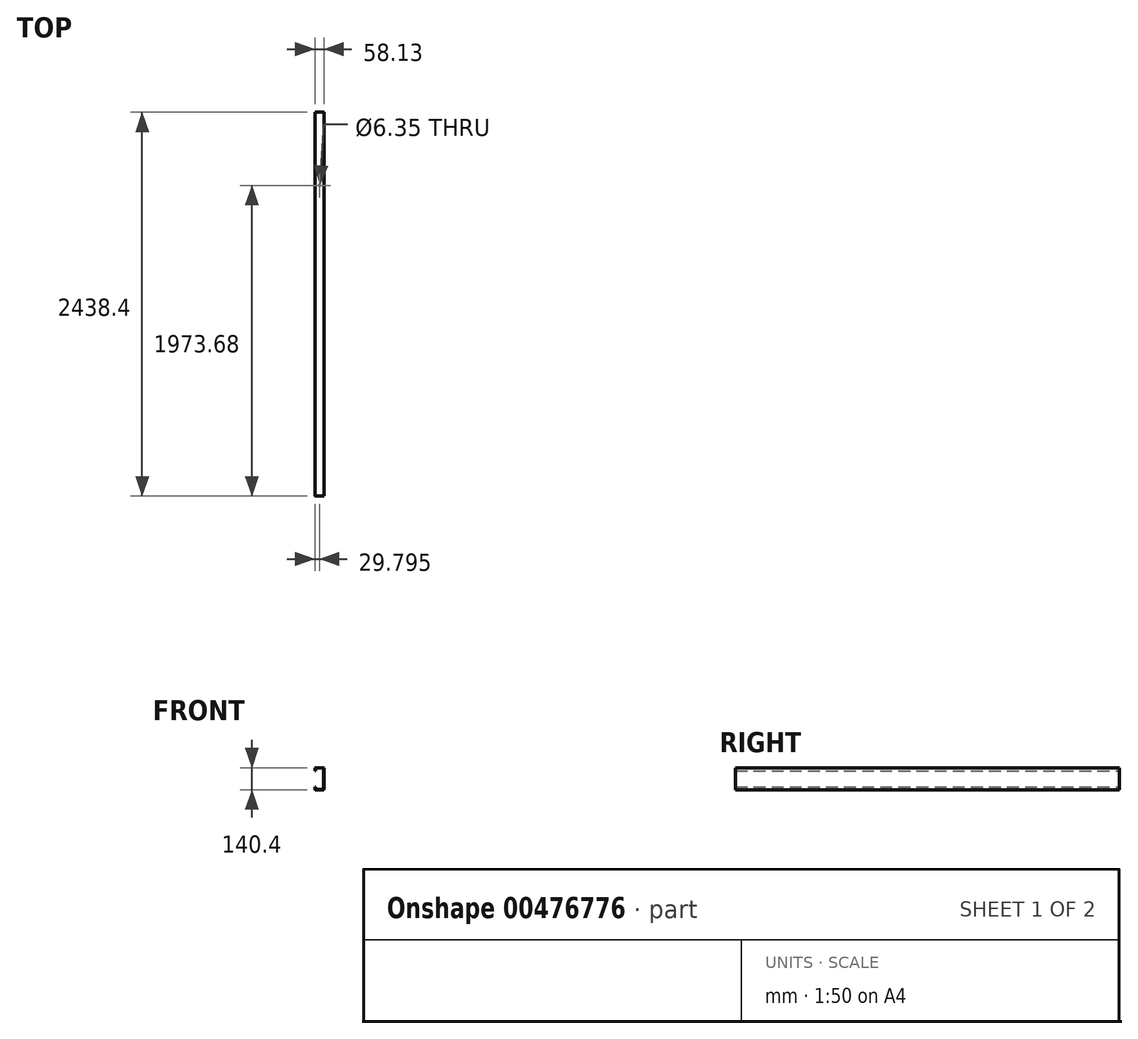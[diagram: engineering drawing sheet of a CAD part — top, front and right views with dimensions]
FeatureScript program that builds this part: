
annotation { "Feature Type Name" : "Feature", "Feature Type Description" : "" }
export const myFeature = defineFeature(function(context is Context, id is Id, definition is map)
    precondition{}
    {
        {
            var Q0;
            Q0=qCreatedBy(makeId("Front.planeOp"),FACE);
            var sketch = newSketch(context, id + "F0", { "sketchPlane" : qUnion([Q0])});
            skLineSegment(sketch, "E0", {"start": v(-431.8, -558.8) * mm, "end": v(431.8, -558.8) * mm});
            skLineSegment(sketch, "E1", {"start": v(431.8, -558.8) * mm, "end": v(431.8, 558.8) * mm});
            skLineSegment(sketch, "E2", {"start": v(431.8, 558.8) * mm, "end": v(-431.8, 558.8) * mm});
            skLineSegment(sketch, "E3", {"start": v(-431.8, 558.8) * mm, "end": v(-431.8, -558.8) * mm});
            skLineSegment(sketch, "E4", {"start": v(-381, -504.83) * mm, "end": v(381, -504.83) * mm});
            skLineSegment(sketch, "E5", {"start": v(381, -504.83) * mm, "end": v(381, 504.83) * mm});
            skLineSegment(sketch, "E6", {"start": v(381, 504.83) * mm, "end": v(360.7, 504.83) * mm});
            skLineSegment(sketch, "E7", {"start": v(265.82, 504.83) * mm, "end": v(-381, 504.83) * mm});
            skLineSegment(sketch, "E8", {"start": v(-381, 504.83) * mm, "end": v(-381, -504.83) * mm});
            skLineSegment(sketch, "E9", {"start": v(-381, -403.23) * mm, "end": v(381, -403.23) * mm});
            skLineSegment(sketch, "E10", {"start": v(-152.4, -403.23) * mm, "end": v(-152.4, -504.83) * mm});
            skLineSegment(sketch, "E11", {"start": v(152.4, -403.23) * mm, "end": v(152.4, -504.83) * mm});
            skLineSegment(sketch, "E12", {"start": v(349.12, 503.33) * mm, "end": v(324.77, 544.8) * mm});
            skLineSegment(sketch, "E13", {"start": v(324.92, 525.17) * mm, "end": v(343.26, 493.25) * mm});
            skLineSegment(sketch, "E14", {"start": v(345.3, 496.77) * mm, "end": v(323.11, 534.57) * mm});
            skLineSegment(sketch, "E15", {"start": v(351.17, 506.85) * mm, "end": v(327.06, 548.5) * mm});
            skLineSegment(sketch, "E16", {"start": v(335.24, 486.66) * mm, "end": v(339.43, 486.66) * mm});
            skLineSegment(sketch, "E17", {"start": v(323.53, 514.34) * mm, "end": v(339.43, 486.66) * mm});
            skLineSegment(sketch, "E18", {"start": v(324.77, 544.8) * mm, "end": v(303.2, 507.27) * mm});
            skLineSegment(sketch, "E19", {"start": v(323.11, 534.57) * mm, "end": v(305.2, 503.47) * mm});
            skLineSegment(sketch, "E20", {"start": v(303.02, 548.5) * mm, "end": v(279.32, 507.27) * mm});
            skLineSegment(sketch, "E21", {"start": v(305.2, 503.47) * mm, "end": v(281.51, 503.47) * mm});
            skLineSegment(sketch, "E22", {"start": v(303.2, 507.27) * mm, "end": v(279.32, 507.27) * mm});
            skLineSegment(sketch, "E23", {"start": v(287.46, 493.17) * mm, "end": v(311.53, 493.17) * mm});
            skLineSegment(sketch, "E24", {"start": v(285.48, 496.6) * mm, "end": v(309, 496.6) * mm});
            skLineSegment(sketch, "E25", {"start": v(315.3, 486.66) * mm, "end": v(291.22, 486.66) * mm});
            skLineSegment(sketch, "E26", {"start": v(281.51, 503.47) * mm, "end": v(285.48, 496.6) * mm});
            skLineSegment(sketch, "E27", {"start": v(287.46, 493.17) * mm, "end": v(291.22, 486.66) * mm});
            skLineSegment(sketch, "E28", {"start": v(309, 496.6) * mm, "end": v(324.92, 525.17) * mm});
            skLineSegment(sketch, "E29", {"start": v(311.53, 493.17) * mm, "end": v(323.53, 514.34) * mm});
            skLineSegment(sketch, "E30", {"start": v(325.28, 503.65) * mm, "end": v(315.3, 486.66) * mm});
            skLineSegment(sketch, "E31", {"start": v(319.7, 486.66) * mm, "end": v(326.89, 486.66) * mm});
            skLineSegment(sketch, "E32", {"start": v(319.7, 486.66) * mm, "end": v(323.3, 492.99) * mm});
            skLineSegment(sketch, "E33", {"start": v(335.24, 486.66) * mm, "end": v(325.28, 503.65) * mm});
            skLineSegment(sketch, "E34", {"start": v(323.3, 492.99) * mm, "end": v(326.89, 486.66) * mm});
            skLineSegment(sketch, "E35", {"start": v(327.06, 548.5) * mm, "end": v(303.02, 548.5) * mm});
            skLineSegment(sketch, "E36", {"start": v(343.26, 493.25) * mm, "end": v(345.3, 496.77) * mm});
            skLineSegment(sketch, "E37", {"start": v(349.12, 503.33) * mm, "end": v(351.17, 506.85) * mm});
            skCircle(sketch, "E38", {"center": v(350.6, 458.79) * mm, "radius": 1.85 * mm});
            skLineSegment(sketch, "E39", {"start": v(-201.65, 389.86) * mm, "end": v(-204.7, 389.86) * mm});
            skLineSegment(sketch, "E40", {"start": v(-201.65, 287.56) * mm, "end": v(-204.7, 287.56) * mm});
            skLineSegment(sketch, "E41", {"start": v(-204.7, 389.86) * mm, "end": v(-204.7, 405.1) * mm});
            skLineSegment(sketch, "E42", {"start": v(-201.65, 389.86) * mm, "end": v(-201.65, 405.1) * mm});
            skArc(sketch, "E43", {"start": v(-200.89, 405.86) * mm, "mid": v(-201.43, 405.64) * mm, "end": v(-201.65, 405.1) * mm});
            skArc(sketch, "E44", {"start": v(-200.89, 408.9) * mm, "mid": v(-203.58, 407.8) * mm, "end": v(-204.7, 405.1) * mm});
            skLineSegment(sketch, "E45", {"start": v(-200.89, 408.9) * mm, "end": v(-151.83, 408.9) * mm});
            skLineSegment(sketch, "E46", {"start": v(-200.89, 405.86) * mm, "end": v(-151.83, 405.86) * mm});
            skArc(sketch, "E47", {"start": v(-151.07, 405.1) * mm, "mid": v(-151.3, 405.64) * mm, "end": v(-151.83, 405.86) * mm});
            skArc(sketch, "E48", {"start": v(-148.02, 405.1) * mm, "mid": v(-149.14, 407.8) * mm, "end": v(-151.83, 408.9) * mm});
            skLineSegment(sketch, "E49", {"start": v(-148.02, 405.1) * mm, "end": v(-148.02, 272.32) * mm});
            skLineSegment(sketch, "E50", {"start": v(-151.07, 405.1) * mm, "end": v(-151.07, 272.32) * mm});
            skLineSegment(sketch, "E51", {"start": v(-204.7, 287.56) * mm, "end": v(-204.7, 273.15) * mm});
            skLineSegment(sketch, "E52", {"start": v(-201.65, 287.56) * mm, "end": v(-201.65, 273.15) * mm});
            skLineSegment(sketch, "E53", {"start": v(-200.06, 268.51) * mm, "end": v(-151.83, 268.51) * mm});
            skLineSegment(sketch, "E54", {"start": v(-200.06, 271.56) * mm, "end": v(-151.83, 271.56) * mm});
            skArc(sketch, "E55", {"start": v(-151.83, 271.56) * mm, "mid": v(-151.3, 271.79) * mm, "end": v(-151.07, 272.32) * mm});
            skArc(sketch, "E56", {"start": v(-151.83, 268.51) * mm, "mid": v(-149.14, 269.63) * mm, "end": v(-148.02, 272.32) * mm});
            skArc(sketch, "E57", {"start": v(-201.65, 273.15) * mm, "mid": v(-201.19, 272.03) * mm, "end": v(-200.06, 271.56) * mm});
            skArc(sketch, "E58", {"start": v(-204.7, 273.15) * mm, "mid": v(-203.34, 269.87) * mm, "end": v(-200.06, 268.51) * mm});
            skLineSegment(sketch, "E59", {"start": v(268.24, 192.18) * mm, "end": v(-275.4, 192.18) * mm});
            skLineSegment(sketch, "E60", {"start": v(-275.4, 267.58) * mm, "end": v(268.24, 267.58) * mm});
            skLineSegment(sketch, "E61", {"start": v(-275.4, 191.38) * mm, "end": v(268.24, 191.38) * mm});
            skLineSegment(sketch, "E62", {"start": v(-275.4, 189.56) * mm, "end": v(-275.4, 233.5) * mm});
            skLineSegment(sketch, "E63", {"start": v(-275.4, 238.46) * mm, "end": v(-275.4, 270.12) * mm});
            skLineSegment(sketch, "E64", {"start": v(-275.4, 233.5) * mm, "end": v(-264.27, 236) * mm});
            skLineSegment(sketch, "E65", {"start": v(-287.59, 236) * mm, "end": v(-275.4, 238.46) * mm});
            skLineSegment(sketch, "E66", {"start": v(-287.59, 236) * mm, "end": v(-264.27, 236) * mm});
            skLineSegment(sketch, "E67", {"start": v(268.24, 189.56) * mm, "end": v(268.24, 233.5) * mm});
            skLineSegment(sketch, "E68", {"start": v(268.24, 238.46) * mm, "end": v(268.24, 270.12) * mm});
            skLineSegment(sketch, "E69", {"start": v(268.24, 233.5) * mm, "end": v(279.38, 236) * mm});
            skLineSegment(sketch, "E70", {"start": v(256.06, 236) * mm, "end": v(268.24, 238.46) * mm});
            skLineSegment(sketch, "E71", {"start": v(256.06, 236) * mm, "end": v(279.38, 236) * mm});
            skLineSegment(sketch, "E72", {"start": v(267.92, 175.66) * mm, "end": v(267.92, 187.92) * mm});
            skLineSegment(sketch, "E73", {"start": v(-275.4, 175.66) * mm, "end": v(-275.4, 187.92) * mm});
            skLineSegment(sketch, "E74", {"start": v(131.2, 389.86) * mm, "end": v(128.15, 389.86) * mm});
            skLineSegment(sketch, "E75", {"start": v(131.2, 287.54) * mm, "end": v(128.15, 287.54) * mm});
            skLineSegment(sketch, "E76", {"start": v(128.15, 389.86) * mm, "end": v(128.15, 405.1) * mm});
            skLineSegment(sketch, "E77", {"start": v(131.2, 389.86) * mm, "end": v(131.2, 405.1) * mm});
            skArc(sketch, "E78", {"start": v(131.96, 408.9) * mm, "mid": v(129.27, 407.8) * mm, "end": v(128.15, 405.1) * mm});
            skLineSegment(sketch, "E79", {"start": v(131.96, 408.9) * mm, "end": v(182.96, 408.9) * mm});
            skLineSegment(sketch, "E80", {"start": v(131.96, 405.86) * mm, "end": v(182.96, 405.86) * mm});
            skArc(sketch, "E81", {"start": v(183.72, 405.1) * mm, "mid": v(183.5, 405.64) * mm, "end": v(182.96, 405.86) * mm});
            skArc(sketch, "E82", {"start": v(186.77, 405.1) * mm, "mid": v(185.65, 407.8) * mm, "end": v(182.96, 408.9) * mm});
            skLineSegment(sketch, "E83", {"start": v(186.77, 405.1) * mm, "end": v(186.77, 272.3) * mm});
            skLineSegment(sketch, "E84", {"start": v(183.72, 405.1) * mm, "end": v(183.72, 272.3) * mm});
            skLineSegment(sketch, "E85", {"start": v(128.15, 287.54) * mm, "end": v(128.15, 273.12) * mm});
            skLineSegment(sketch, "E86", {"start": v(131.2, 287.54) * mm, "end": v(131.2, 273.12) * mm});
            skLineSegment(sketch, "E87", {"start": v(132.79, 268.49) * mm, "end": v(182.96, 268.49) * mm});
            skLineSegment(sketch, "E88", {"start": v(132.79, 271.53) * mm, "end": v(182.96, 271.53) * mm});
            skArc(sketch, "E89", {"start": v(182.96, 271.53) * mm, "mid": v(183.5, 271.76) * mm, "end": v(183.72, 272.3) * mm});
            skArc(sketch, "E90", {"start": v(182.96, 268.49) * mm, "mid": v(185.65, 269.6) * mm, "end": v(186.77, 272.3) * mm});
            skArc(sketch, "E91", {"start": v(131.2, 273.12) * mm, "mid": v(131.67, 272) * mm, "end": v(132.79, 271.53) * mm});
            skArc(sketch, "E92", {"start": v(128.15, 273.12) * mm, "mid": v(129.51, 269.84) * mm, "end": v(132.79, 268.49) * mm});
            skLineSegment(sketch, "E93", {"start": v(-275.4, 266.78) * mm, "end": v(268.24, 266.78) * mm});
            skArc(sketch, "E94", {"start": v(131.96, 405.86) * mm, "mid": v(131.42, 405.64) * mm, "end": v(131.2, 405.1) * mm});
            skLineSegment(sketch, "E95", {"start": v(-148.02, 350.55) * mm, "end": v(-147.38, 350.55) * mm});
            skLineSegment(sketch, "E96", {"start": v(268.24, 220.63) * mm, "end": v(-275.4, 220.63) * mm});
            skLineSegment(sketch, "E97", {"start": v(-275.4, 219.83) * mm, "end": v(268.24, 219.83) * mm});
            skLineSegment(sketch, "E98", {"start": v(111.4, 219.88) * mm, "end": v(200.2, 219.88) * mm});
            skLineSegment(sketch, "E99", {"start": v(200.2, 219.88) * mm, "end": v(200.2, 218.1) * mm});
            skLineSegment(sketch, "E100", {"start": v(111.4, 219.88) * mm, "end": v(111.4, 218.1) * mm});
            skLineSegment(sketch, "E101", {"start": v(111.4, 218.1) * mm, "end": v(200.2, 218.1) * mm});
            skLineSegment(sketch, "E102", {"start": v(165.87, 216.24) * mm, "end": v(165.87, 217.5) * mm});
            skLineSegment(sketch, "E103", {"start": v(152.66, 216.24) * mm, "end": v(152.66, 217.5) * mm});
            skLineSegment(sketch, "E104", {"start": v(164.46, 211.81) * mm, "end": v(164.46, 216.24) * mm});
            skLineSegment(sketch, "E105", {"start": v(154.07, 211.81) * mm, "end": v(154.07, 216.24) * mm});
            skLineSegment(sketch, "E106", {"start": v(161.7, 259.32) * mm, "end": v(161.7, 260.34) * mm});
            skLineSegment(sketch, "E107", {"start": v(161.7, 261.14) * mm, "end": v(161.7, 262.16) * mm});
            skLineSegment(sketch, "E108", {"start": v(161.7, 262.95) * mm, "end": v(161.7, 263.97) * mm});
            skLineSegment(sketch, "E109", {"start": v(161.7, 264.76) * mm, "end": v(161.7, 265.78) * mm});
            skLineSegment(sketch, "E110", {"start": v(161.7, 266.58) * mm, "end": v(161.7, 267.6) * mm});
            skLineSegment(sketch, "E111", {"start": v(161.7, 268.39) * mm, "end": v(161.7, 269.41) * mm});
            skLineSegment(sketch, "E112", {"start": v(161.7, 270.2) * mm, "end": v(161.7, 271.22) * mm});
            skLineSegment(sketch, "E113", {"start": v(161.7, 272.02) * mm, "end": v(161.7, 273.04) * mm});
            skLineSegment(sketch, "E114", {"start": v(161.7, 273.83) * mm, "end": v(161.7, 274.85) * mm});
            skLineSegment(sketch, "E115", {"start": v(161.7, 275.64) * mm, "end": v(161.7, 276.67) * mm});
            skLineSegment(sketch, "E116", {"start": v(161.7, 277.46) * mm, "end": v(161.7, 278.48) * mm});
            skLineSegment(sketch, "E117", {"start": v(156.83, 257.5) * mm, "end": v(156.83, 258.53) * mm});
            skLineSegment(sketch, "E118", {"start": v(156.83, 259.32) * mm, "end": v(156.83, 260.34) * mm});
            skLineSegment(sketch, "E119", {"start": v(156.83, 261.14) * mm, "end": v(156.83, 262.16) * mm});
            skLineSegment(sketch, "E120", {"start": v(156.83, 262.95) * mm, "end": v(156.83, 263.97) * mm});
            skLineSegment(sketch, "E121", {"start": v(156.83, 264.76) * mm, "end": v(156.83, 265.78) * mm});
            skLineSegment(sketch, "E122", {"start": v(156.83, 266.58) * mm, "end": v(156.83, 267.6) * mm});
            skLineSegment(sketch, "E123", {"start": v(156.83, 268.39) * mm, "end": v(156.83, 269.41) * mm});
            skLineSegment(sketch, "E124", {"start": v(156.83, 270.2) * mm, "end": v(156.83, 271.22) * mm});
            skLineSegment(sketch, "E125", {"start": v(156.83, 272.02) * mm, "end": v(156.83, 273.04) * mm});
            skLineSegment(sketch, "E126", {"start": v(156.83, 273.83) * mm, "end": v(156.83, 274.85) * mm});
            skLineSegment(sketch, "E127", {"start": v(156.83, 275.64) * mm, "end": v(156.83, 276.67) * mm});
            skLineSegment(sketch, "E128", {"start": v(156.14, 258.93) * mm, "end": v(156.83, 258.53) * mm});
            skLineSegment(sketch, "E129", {"start": v(156.14, 258.93) * mm, "end": v(156.83, 259.32) * mm});
            skLineSegment(sketch, "E130", {"start": v(156.14, 260.74) * mm, "end": v(156.83, 260.34) * mm});
            skLineSegment(sketch, "E131", {"start": v(156.14, 260.74) * mm, "end": v(156.83, 261.14) * mm});
            skLineSegment(sketch, "E132", {"start": v(162.39, 260.74) * mm, "end": v(161.7, 260.34) * mm});
            skLineSegment(sketch, "E133", {"start": v(162.39, 260.74) * mm, "end": v(161.7, 261.14) * mm});
            skLineSegment(sketch, "E134", {"start": v(162.39, 262.55) * mm, "end": v(161.7, 262.16) * mm});
            skLineSegment(sketch, "E135", {"start": v(162.39, 262.55) * mm, "end": v(161.7, 262.95) * mm});
            skLineSegment(sketch, "E136", {"start": v(156.14, 258.93) * mm, "end": v(162.39, 260.74) * mm});
            skLineSegment(sketch, "E137", {"start": v(156.14, 260.74) * mm, "end": v(162.39, 262.55) * mm});
            skLineSegment(sketch, "E138", {"start": v(156.83, 258.53) * mm, "end": v(161.7, 260.34) * mm});
            skLineSegment(sketch, "E139", {"start": v(156.83, 259.32) * mm, "end": v(161.7, 261.14) * mm});
            skLineSegment(sketch, "E140", {"start": v(156.83, 260.34) * mm, "end": v(161.7, 262.16) * mm});
            skLineSegment(sketch, "E141", {"start": v(156.83, 261.14) * mm, "end": v(161.7, 262.95) * mm});
            skLineSegment(sketch, "E142", {"start": v(156.14, 262.55) * mm, "end": v(156.83, 262.16) * mm});
            skLineSegment(sketch, "E143", {"start": v(156.14, 262.55) * mm, "end": v(156.83, 262.95) * mm});
            skLineSegment(sketch, "E144", {"start": v(156.14, 264.37) * mm, "end": v(156.83, 263.97) * mm});
            skLineSegment(sketch, "E145", {"start": v(156.14, 264.37) * mm, "end": v(156.83, 264.76) * mm});
            skLineSegment(sketch, "E146", {"start": v(162.39, 264.37) * mm, "end": v(161.7, 263.97) * mm});
            skLineSegment(sketch, "E147", {"start": v(162.39, 264.37) * mm, "end": v(161.7, 264.76) * mm});
            skLineSegment(sketch, "E148", {"start": v(162.39, 266.18) * mm, "end": v(161.7, 265.78) * mm});
            skLineSegment(sketch, "E149", {"start": v(162.39, 266.18) * mm, "end": v(161.7, 266.58) * mm});
            skLineSegment(sketch, "E150", {"start": v(156.14, 262.55) * mm, "end": v(162.39, 264.37) * mm});
            skLineSegment(sketch, "E151", {"start": v(156.14, 264.37) * mm, "end": v(162.39, 266.18) * mm});
            skLineSegment(sketch, "E152", {"start": v(156.83, 262.16) * mm, "end": v(161.7, 263.97) * mm});
            skLineSegment(sketch, "E153", {"start": v(156.83, 262.95) * mm, "end": v(161.7, 264.76) * mm});
            skLineSegment(sketch, "E154", {"start": v(156.83, 263.97) * mm, "end": v(161.7, 265.78) * mm});
            skLineSegment(sketch, "E155", {"start": v(156.83, 264.76) * mm, "end": v(161.7, 266.58) * mm});
            skLineSegment(sketch, "E156", {"start": v(156.14, 266.18) * mm, "end": v(156.83, 265.78) * mm});
            skLineSegment(sketch, "E157", {"start": v(156.14, 266.18) * mm, "end": v(156.83, 266.58) * mm});
            skLineSegment(sketch, "E158", {"start": v(162.39, 268) * mm, "end": v(161.7, 267.6) * mm});
            skLineSegment(sketch, "E159", {"start": v(162.39, 268) * mm, "end": v(161.7, 268.39) * mm});
            skLineSegment(sketch, "E160", {"start": v(156.14, 266.18) * mm, "end": v(162.39, 268) * mm});
            skLineSegment(sketch, "E161", {"start": v(156.83, 265.78) * mm, "end": v(161.7, 267.6) * mm});
            skLineSegment(sketch, "E162", {"start": v(156.83, 266.58) * mm, "end": v(161.7, 268.39) * mm});
            skLineSegment(sketch, "E163", {"start": v(156.14, 268) * mm, "end": v(156.83, 267.6) * mm});
            skLineSegment(sketch, "E164", {"start": v(156.14, 268) * mm, "end": v(156.83, 268.39) * mm});
            skLineSegment(sketch, "E165", {"start": v(156.14, 269.8) * mm, "end": v(156.83, 269.41) * mm});
            skLineSegment(sketch, "E166", {"start": v(156.14, 269.8) * mm, "end": v(156.83, 270.2) * mm});
            skLineSegment(sketch, "E167", {"start": v(162.39, 269.8) * mm, "end": v(161.7, 269.41) * mm});
            skLineSegment(sketch, "E168", {"start": v(162.39, 269.8) * mm, "end": v(161.7, 270.2) * mm});
            skLineSegment(sketch, "E169", {"start": v(162.39, 271.62) * mm, "end": v(161.7, 271.22) * mm});
            skLineSegment(sketch, "E170", {"start": v(162.39, 271.62) * mm, "end": v(161.7, 272.02) * mm});
            skLineSegment(sketch, "E171", {"start": v(156.14, 268) * mm, "end": v(162.39, 269.8) * mm});
            skLineSegment(sketch, "E172", {"start": v(156.14, 269.8) * mm, "end": v(162.39, 271.62) * mm});
            skLineSegment(sketch, "E173", {"start": v(156.83, 267.6) * mm, "end": v(161.7, 269.41) * mm});
            skLineSegment(sketch, "E174", {"start": v(156.83, 268.39) * mm, "end": v(161.7, 270.2) * mm});
            skLineSegment(sketch, "E175", {"start": v(156.83, 269.41) * mm, "end": v(161.7, 271.22) * mm});
            skLineSegment(sketch, "E176", {"start": v(156.83, 270.2) * mm, "end": v(161.7, 272.02) * mm});
            skLineSegment(sketch, "E177", {"start": v(156.14, 271.62) * mm, "end": v(156.83, 271.22) * mm});
            skLineSegment(sketch, "E178", {"start": v(156.14, 271.62) * mm, "end": v(156.83, 272.02) * mm});
            skLineSegment(sketch, "E179", {"start": v(156.14, 273.43) * mm, "end": v(156.83, 273.04) * mm});
            skLineSegment(sketch, "E180", {"start": v(156.14, 273.43) * mm, "end": v(156.83, 273.83) * mm});
            skLineSegment(sketch, "E181", {"start": v(162.39, 273.43) * mm, "end": v(161.7, 273.04) * mm});
            skLineSegment(sketch, "E182", {"start": v(162.39, 273.43) * mm, "end": v(161.7, 273.83) * mm});
            skLineSegment(sketch, "E183", {"start": v(162.39, 275.25) * mm, "end": v(161.7, 274.85) * mm});
            skLineSegment(sketch, "E184", {"start": v(162.39, 275.25) * mm, "end": v(161.7, 275.64) * mm});
            skLineSegment(sketch, "E185", {"start": v(156.14, 271.62) * mm, "end": v(162.39, 273.43) * mm});
            skLineSegment(sketch, "E186", {"start": v(156.14, 273.43) * mm, "end": v(162.39, 275.25) * mm});
            skLineSegment(sketch, "E187", {"start": v(156.83, 271.22) * mm, "end": v(161.7, 273.04) * mm});
            skLineSegment(sketch, "E188", {"start": v(156.83, 272.02) * mm, "end": v(161.7, 273.83) * mm});
            skLineSegment(sketch, "E189", {"start": v(156.83, 273.04) * mm, "end": v(161.7, 274.85) * mm});
            skLineSegment(sketch, "E190", {"start": v(156.83, 273.83) * mm, "end": v(161.7, 275.64) * mm});
            skLineSegment(sketch, "E191", {"start": v(156.14, 275.25) * mm, "end": v(156.83, 274.85) * mm});
            skLineSegment(sketch, "E192", {"start": v(156.14, 275.25) * mm, "end": v(156.83, 275.64) * mm});
            skLineSegment(sketch, "E193", {"start": v(156.14, 277.06) * mm, "end": v(156.83, 276.67) * mm});
            skLineSegment(sketch, "E194", {"start": v(156.14, 277.06) * mm, "end": v(156.83, 277.46) * mm});
            skLineSegment(sketch, "E195", {"start": v(162.39, 277.06) * mm, "end": v(161.7, 276.67) * mm});
            skLineSegment(sketch, "E196", {"start": v(162.39, 277.06) * mm, "end": v(161.7, 277.46) * mm});
            skLineSegment(sketch, "E197", {"start": v(162.39, 278.87) * mm, "end": v(161.7, 278.48) * mm});
            skLineSegment(sketch, "E198", {"start": v(162.39, 278.87) * mm, "end": v(161.7, 279.27) * mm});
            skLineSegment(sketch, "E199", {"start": v(156.14, 275.25) * mm, "end": v(162.39, 277.06) * mm});
            skLineSegment(sketch, "E200", {"start": v(156.14, 277.06) * mm, "end": v(162.39, 278.87) * mm});
            skLineSegment(sketch, "E201", {"start": v(156.83, 274.85) * mm, "end": v(161.7, 276.67) * mm});
            skLineSegment(sketch, "E202", {"start": v(156.83, 275.64) * mm, "end": v(161.7, 277.46) * mm});
            skLineSegment(sketch, "E203", {"start": v(156.83, 276.67) * mm, "end": v(161.7, 278.48) * mm});
            skLineSegment(sketch, "E204", {"start": v(156.83, 277.46) * mm, "end": v(161.7, 279.27) * mm});
            skLineSegment(sketch, "E205", {"start": v(152.66, 217.5) * mm, "end": v(165.87, 217.5) * mm});
            skLineSegment(sketch, "E206", {"start": v(152.66, 216.24) * mm, "end": v(165.87, 216.24) * mm});
            skLineSegment(sketch, "E207", {"start": v(154.77, 211.41) * mm, "end": v(163.76, 211.41) * mm});
            skLineSegment(sketch, "E208", {"start": v(156.67, 211.81) * mm, "end": v(156.67, 216.24) * mm});
            skLineSegment(sketch, "E209", {"start": v(161.86, 211.81) * mm, "end": v(161.86, 216.24) * mm});
            skLineSegment(sketch, "E210", {"start": v(154.77, 211.41) * mm, "end": v(154.07, 211.81) * mm});
            skLineSegment(sketch, "E211", {"start": v(163.76, 211.41) * mm, "end": v(164.46, 211.81) * mm});
            skLineSegment(sketch, "E212", {"start": v(161.16, 211.41) * mm, "end": v(161.86, 211.81) * mm});
            skLineSegment(sketch, "E213", {"start": v(155.97, 211.41) * mm, "end": v(156.67, 211.81) * mm});
            skLineSegment(sketch, "E214", {"start": v(162.56, 211.41) * mm, "end": v(161.86, 211.81) * mm});
            skLineSegment(sketch, "E215", {"start": v(157.36, 211.41) * mm, "end": v(156.67, 211.81) * mm});
            skLineSegment(sketch, "E216", {"start": v(156.83, 277.46) * mm, "end": v(156.83, 288.94) * mm});
            skLineSegment(sketch, "E217", {"start": v(161.05, 279.03) * mm, "end": v(161.05, 288.94) * mm});
            skLineSegment(sketch, "E218", {"start": v(158.94, 290.16) * mm, "end": v(156.83, 288.94) * mm});
            skLineSegment(sketch, "E219", {"start": v(158.94, 290.16) * mm, "end": v(161.05, 288.94) * mm});
            skLineSegment(sketch, "E220", {"start": v(158.94, 290.16) * mm, "end": v(158.94, 280.63) * mm});
            skArc(sketch, "E221", {"start": v(158.94, 280.63) * mm, "mid": v(159.28, 279.49) * mm, "end": v(160.18, 278.7) * mm});
            skLineSegment(sketch, "E222", {"start": v(156.14, 257.11) * mm, "end": v(156.83, 256.72) * mm});
            skLineSegment(sketch, "E223", {"start": v(156.14, 257.11) * mm, "end": v(156.83, 257.5) * mm});
            skLineSegment(sketch, "E224", {"start": v(162.39, 258.93) * mm, "end": v(161.7, 258.53) * mm});
            skLineSegment(sketch, "E225", {"start": v(162.39, 258.93) * mm, "end": v(161.7, 259.32) * mm});
            skLineSegment(sketch, "E226", {"start": v(156.14, 257.11) * mm, "end": v(162.39, 258.93) * mm});
            skLineSegment(sketch, "E227", {"start": v(156.83, 256.72) * mm, "end": v(161.7, 258.53) * mm});
            skLineSegment(sketch, "E228", {"start": v(156.83, 257.5) * mm, "end": v(161.7, 259.32) * mm});
            skLineSegment(sketch, "E229", {"start": v(156.83, 256.72) * mm, "end": v(156.83, 217.5) * mm});
            skLineSegment(sketch, "E230", {"start": v(161.7, 258.53) * mm, "end": v(161.7, 217.5) * mm});
            skLineSegment(sketch, "E231", {"start": v(-224.84, 219.88) * mm, "end": v(-136.05, 219.88) * mm});
            skLineSegment(sketch, "E232", {"start": v(-224.84, 218.1) * mm, "end": v(-136.05, 218.1) * mm});
            skLineSegment(sketch, "E233", {"start": v(-136.05, 219.88) * mm, "end": v(-136.05, 218.1) * mm});
            skLineSegment(sketch, "E234", {"start": v(-224.84, 219.88) * mm, "end": v(-224.84, 218.1) * mm});
            skLineSegment(sketch, "E235", {"start": v(-170.37, 216.24) * mm, "end": v(-170.37, 217.5) * mm});
            skLineSegment(sketch, "E236", {"start": v(-183.58, 216.24) * mm, "end": v(-183.58, 217.5) * mm});
            skLineSegment(sketch, "E237", {"start": v(-171.78, 211.81) * mm, "end": v(-171.78, 216.24) * mm});
            skLineSegment(sketch, "E238", {"start": v(-182.17, 211.81) * mm, "end": v(-182.17, 216.24) * mm});
            skLineSegment(sketch, "E239", {"start": v(-174.54, 259.32) * mm, "end": v(-174.54, 260.34) * mm});
            skLineSegment(sketch, "E240", {"start": v(-174.54, 261.14) * mm, "end": v(-174.54, 262.16) * mm});
            skLineSegment(sketch, "E241", {"start": v(-174.54, 262.95) * mm, "end": v(-174.54, 263.97) * mm});
            skLineSegment(sketch, "E242", {"start": v(-174.54, 264.76) * mm, "end": v(-174.54, 265.78) * mm});
            skLineSegment(sketch, "E243", {"start": v(-174.54, 266.58) * mm, "end": v(-174.54, 267.6) * mm});
            skLineSegment(sketch, "E244", {"start": v(-174.54, 268.39) * mm, "end": v(-174.54, 269.41) * mm});
            skLineSegment(sketch, "E245", {"start": v(-174.54, 270.2) * mm, "end": v(-174.54, 271.22) * mm});
            skLineSegment(sketch, "E246", {"start": v(-174.54, 272.02) * mm, "end": v(-174.54, 273.04) * mm});
            skLineSegment(sketch, "E247", {"start": v(-174.54, 273.83) * mm, "end": v(-174.54, 274.85) * mm});
            skLineSegment(sketch, "E248", {"start": v(-174.54, 275.64) * mm, "end": v(-174.54, 276.67) * mm});
            skLineSegment(sketch, "E249", {"start": v(-174.54, 277.46) * mm, "end": v(-174.54, 278.48) * mm});
            skLineSegment(sketch, "E250", {"start": v(-179.41, 257.5) * mm, "end": v(-179.41, 258.53) * mm});
            skLineSegment(sketch, "E251", {"start": v(-179.41, 259.32) * mm, "end": v(-179.41, 260.34) * mm});
            skLineSegment(sketch, "E252", {"start": v(-179.41, 261.14) * mm, "end": v(-179.41, 262.16) * mm});
            skLineSegment(sketch, "E253", {"start": v(-179.41, 262.95) * mm, "end": v(-179.41, 263.97) * mm});
            skLineSegment(sketch, "E254", {"start": v(-179.41, 264.76) * mm, "end": v(-179.41, 265.78) * mm});
            skLineSegment(sketch, "E255", {"start": v(-179.41, 266.58) * mm, "end": v(-179.41, 267.6) * mm});
            skLineSegment(sketch, "E256", {"start": v(-179.41, 268.39) * mm, "end": v(-179.41, 269.41) * mm});
            skLineSegment(sketch, "E257", {"start": v(-179.41, 270.2) * mm, "end": v(-179.41, 271.22) * mm});
            skLineSegment(sketch, "E258", {"start": v(-179.41, 272.02) * mm, "end": v(-179.41, 273.04) * mm});
            skLineSegment(sketch, "E259", {"start": v(-179.41, 273.83) * mm, "end": v(-179.41, 274.85) * mm});
            skLineSegment(sketch, "E260", {"start": v(-179.41, 275.64) * mm, "end": v(-179.41, 276.67) * mm});
            skLineSegment(sketch, "E261", {"start": v(-180.1, 258.93) * mm, "end": v(-179.41, 258.53) * mm});
            skLineSegment(sketch, "E262", {"start": v(-180.1, 258.93) * mm, "end": v(-179.41, 259.32) * mm});
            skLineSegment(sketch, "E263", {"start": v(-180.1, 260.74) * mm, "end": v(-179.41, 260.34) * mm});
            skLineSegment(sketch, "E264", {"start": v(-180.1, 260.74) * mm, "end": v(-179.41, 261.14) * mm});
            skLineSegment(sketch, "E265", {"start": v(-173.85, 260.74) * mm, "end": v(-174.54, 260.34) * mm});
            skLineSegment(sketch, "E266", {"start": v(-173.85, 260.74) * mm, "end": v(-174.54, 261.14) * mm});
            skLineSegment(sketch, "E267", {"start": v(-173.85, 262.55) * mm, "end": v(-174.54, 262.16) * mm});
            skLineSegment(sketch, "E268", {"start": v(-173.85, 262.55) * mm, "end": v(-174.54, 262.95) * mm});
            skLineSegment(sketch, "E269", {"start": v(-180.1, 258.93) * mm, "end": v(-173.85, 260.74) * mm});
            skLineSegment(sketch, "E270", {"start": v(-180.1, 260.74) * mm, "end": v(-173.85, 262.55) * mm});
            skLineSegment(sketch, "E271", {"start": v(-179.41, 258.53) * mm, "end": v(-174.54, 260.34) * mm});
            skLineSegment(sketch, "E272", {"start": v(-179.41, 259.32) * mm, "end": v(-174.54, 261.14) * mm});
            skLineSegment(sketch, "E273", {"start": v(-179.41, 260.34) * mm, "end": v(-174.54, 262.16) * mm});
            skLineSegment(sketch, "E274", {"start": v(-179.41, 261.14) * mm, "end": v(-174.54, 262.95) * mm});
            skLineSegment(sketch, "E275", {"start": v(-180.1, 262.55) * mm, "end": v(-179.41, 262.16) * mm});
            skLineSegment(sketch, "E276", {"start": v(-180.1, 262.55) * mm, "end": v(-179.41, 262.95) * mm});
            skLineSegment(sketch, "E277", {"start": v(-180.1, 264.37) * mm, "end": v(-179.41, 263.97) * mm});
            skLineSegment(sketch, "E278", {"start": v(-180.1, 264.37) * mm, "end": v(-179.41, 264.76) * mm});
            skLineSegment(sketch, "E279", {"start": v(-173.85, 264.37) * mm, "end": v(-174.54, 263.97) * mm});
            skLineSegment(sketch, "E280", {"start": v(-173.85, 264.37) * mm, "end": v(-174.54, 264.76) * mm});
            skLineSegment(sketch, "E281", {"start": v(-173.85, 266.18) * mm, "end": v(-174.54, 265.78) * mm});
            skLineSegment(sketch, "E282", {"start": v(-173.85, 266.18) * mm, "end": v(-174.54, 266.58) * mm});
            skLineSegment(sketch, "E283", {"start": v(-180.1, 262.55) * mm, "end": v(-173.85, 264.37) * mm});
            skLineSegment(sketch, "E284", {"start": v(-180.1, 264.37) * mm, "end": v(-173.85, 266.18) * mm});
            skLineSegment(sketch, "E285", {"start": v(-179.41, 262.16) * mm, "end": v(-174.54, 263.97) * mm});
            skLineSegment(sketch, "E286", {"start": v(-179.41, 262.95) * mm, "end": v(-174.54, 264.76) * mm});
            skLineSegment(sketch, "E287", {"start": v(-179.41, 263.97) * mm, "end": v(-174.54, 265.78) * mm});
            skLineSegment(sketch, "E288", {"start": v(-179.41, 264.76) * mm, "end": v(-174.54, 266.58) * mm});
            skLineSegment(sketch, "E289", {"start": v(-180.1, 266.18) * mm, "end": v(-179.41, 265.78) * mm});
            skLineSegment(sketch, "E290", {"start": v(-180.1, 266.18) * mm, "end": v(-179.41, 266.58) * mm});
            skLineSegment(sketch, "E291", {"start": v(-173.85, 268) * mm, "end": v(-174.54, 267.6) * mm});
            skLineSegment(sketch, "E292", {"start": v(-173.85, 268) * mm, "end": v(-174.54, 268.39) * mm});
            skLineSegment(sketch, "E293", {"start": v(-180.1, 266.18) * mm, "end": v(-173.85, 268) * mm});
            skLineSegment(sketch, "E294", {"start": v(-179.41, 265.78) * mm, "end": v(-174.54, 267.6) * mm});
            skLineSegment(sketch, "E295", {"start": v(-179.41, 266.58) * mm, "end": v(-174.54, 268.39) * mm});
            skLineSegment(sketch, "E296", {"start": v(-180.1, 268) * mm, "end": v(-179.41, 267.6) * mm});
            skLineSegment(sketch, "E297", {"start": v(-180.1, 268) * mm, "end": v(-179.41, 268.39) * mm});
            skLineSegment(sketch, "E298", {"start": v(-180.1, 269.8) * mm, "end": v(-179.41, 269.41) * mm});
            skLineSegment(sketch, "E299", {"start": v(-180.1, 269.8) * mm, "end": v(-179.41, 270.2) * mm});
            skLineSegment(sketch, "E300", {"start": v(-173.85, 269.8) * mm, "end": v(-174.54, 269.41) * mm});
            skLineSegment(sketch, "E301", {"start": v(-173.85, 269.8) * mm, "end": v(-174.54, 270.2) * mm});
            skLineSegment(sketch, "E302", {"start": v(-173.85, 271.62) * mm, "end": v(-174.54, 271.22) * mm});
            skLineSegment(sketch, "E303", {"start": v(-173.85, 271.62) * mm, "end": v(-174.54, 272.02) * mm});
            skLineSegment(sketch, "E304", {"start": v(-180.1, 268) * mm, "end": v(-173.85, 269.8) * mm});
            skLineSegment(sketch, "E305", {"start": v(-180.1, 269.8) * mm, "end": v(-173.85, 271.62) * mm});
            skLineSegment(sketch, "E306", {"start": v(-179.41, 267.6) * mm, "end": v(-174.54, 269.41) * mm});
            skLineSegment(sketch, "E307", {"start": v(-179.41, 268.39) * mm, "end": v(-174.54, 270.2) * mm});
            skLineSegment(sketch, "E308", {"start": v(-179.41, 269.41) * mm, "end": v(-174.54, 271.22) * mm});
            skLineSegment(sketch, "E309", {"start": v(-179.41, 270.2) * mm, "end": v(-174.54, 272.02) * mm});
            skLineSegment(sketch, "E310", {"start": v(-180.1, 271.62) * mm, "end": v(-179.41, 271.22) * mm});
            skLineSegment(sketch, "E311", {"start": v(-180.1, 271.62) * mm, "end": v(-179.41, 272.02) * mm});
            skLineSegment(sketch, "E312", {"start": v(-180.1, 273.43) * mm, "end": v(-179.41, 273.04) * mm});
            skLineSegment(sketch, "E313", {"start": v(-180.1, 273.43) * mm, "end": v(-179.41, 273.83) * mm});
            skLineSegment(sketch, "E314", {"start": v(-173.85, 273.43) * mm, "end": v(-174.54, 273.04) * mm});
            skLineSegment(sketch, "E315", {"start": v(-173.85, 273.43) * mm, "end": v(-174.54, 273.83) * mm});
            skLineSegment(sketch, "E316", {"start": v(-173.85, 275.25) * mm, "end": v(-174.54, 274.85) * mm});
            skLineSegment(sketch, "E317", {"start": v(-173.85, 275.25) * mm, "end": v(-174.54, 275.64) * mm});
            skLineSegment(sketch, "E318", {"start": v(-180.1, 271.62) * mm, "end": v(-173.85, 273.43) * mm});
            skLineSegment(sketch, "E319", {"start": v(-180.1, 273.43) * mm, "end": v(-173.85, 275.25) * mm});
            skLineSegment(sketch, "E320", {"start": v(-179.41, 271.22) * mm, "end": v(-174.54, 273.04) * mm});
            skLineSegment(sketch, "E321", {"start": v(-179.41, 272.02) * mm, "end": v(-174.54, 273.83) * mm});
            skLineSegment(sketch, "E322", {"start": v(-179.41, 273.04) * mm, "end": v(-174.54, 274.85) * mm});
            skLineSegment(sketch, "E323", {"start": v(-179.41, 273.83) * mm, "end": v(-174.54, 275.64) * mm});
            skLineSegment(sketch, "E324", {"start": v(-180.1, 275.25) * mm, "end": v(-179.41, 274.85) * mm});
            skLineSegment(sketch, "E325", {"start": v(-180.1, 275.25) * mm, "end": v(-179.41, 275.64) * mm});
            skLineSegment(sketch, "E326", {"start": v(-180.1, 277.06) * mm, "end": v(-179.41, 276.67) * mm});
            skLineSegment(sketch, "E327", {"start": v(-180.1, 277.06) * mm, "end": v(-179.41, 277.46) * mm});
            skLineSegment(sketch, "E328", {"start": v(-173.85, 277.06) * mm, "end": v(-174.54, 276.67) * mm});
            skLineSegment(sketch, "E329", {"start": v(-173.85, 277.06) * mm, "end": v(-174.54, 277.46) * mm});
            skLineSegment(sketch, "E330", {"start": v(-173.85, 278.87) * mm, "end": v(-174.54, 278.48) * mm});
            skLineSegment(sketch, "E331", {"start": v(-173.85, 278.87) * mm, "end": v(-174.54, 279.27) * mm});
            skLineSegment(sketch, "E332", {"start": v(-180.1, 275.25) * mm, "end": v(-173.85, 277.06) * mm});
            skLineSegment(sketch, "E333", {"start": v(-180.1, 277.06) * mm, "end": v(-173.85, 278.87) * mm});
            skLineSegment(sketch, "E334", {"start": v(-179.41, 274.85) * mm, "end": v(-174.54, 276.67) * mm});
            skLineSegment(sketch, "E335", {"start": v(-179.41, 275.64) * mm, "end": v(-174.54, 277.46) * mm});
            skLineSegment(sketch, "E336", {"start": v(-179.41, 276.67) * mm, "end": v(-174.54, 278.48) * mm});
            skLineSegment(sketch, "E337", {"start": v(-179.41, 277.46) * mm, "end": v(-174.54, 279.27) * mm});
            skLineSegment(sketch, "E338", {"start": v(-183.58, 217.5) * mm, "end": v(-170.37, 217.5) * mm});
            skLineSegment(sketch, "E339", {"start": v(-183.58, 216.24) * mm, "end": v(-170.37, 216.24) * mm});
            skLineSegment(sketch, "E340", {"start": v(-181.47, 211.41) * mm, "end": v(-172.48, 211.41) * mm});
            skLineSegment(sketch, "E341", {"start": v(-179.57, 211.81) * mm, "end": v(-179.57, 216.24) * mm});
            skLineSegment(sketch, "E342", {"start": v(-174.38, 211.81) * mm, "end": v(-174.38, 216.24) * mm});
            skLineSegment(sketch, "E343", {"start": v(-181.47, 211.41) * mm, "end": v(-182.17, 211.81) * mm});
            skLineSegment(sketch, "E344", {"start": v(-172.48, 211.41) * mm, "end": v(-171.78, 211.81) * mm});
            skLineSegment(sketch, "E345", {"start": v(-175.07, 211.41) * mm, "end": v(-174.38, 211.81) * mm});
            skLineSegment(sketch, "E346", {"start": v(-180.27, 211.41) * mm, "end": v(-179.57, 211.81) * mm});
            skLineSegment(sketch, "E347", {"start": v(-173.68, 211.41) * mm, "end": v(-174.38, 211.81) * mm});
            skLineSegment(sketch, "E348", {"start": v(-178.88, 211.41) * mm, "end": v(-179.57, 211.81) * mm});
            skLineSegment(sketch, "E349", {"start": v(-179.41, 277.46) * mm, "end": v(-179.41, 288.94) * mm});
            skLineSegment(sketch, "E350", {"start": v(-175.19, 279.03) * mm, "end": v(-175.19, 288.94) * mm});
            skLineSegment(sketch, "E351", {"start": v(-177.3, 290.16) * mm, "end": v(-179.41, 288.94) * mm});
            skLineSegment(sketch, "E352", {"start": v(-177.3, 290.16) * mm, "end": v(-175.19, 288.94) * mm});
            skLineSegment(sketch, "E353", {"start": v(-177.3, 290.16) * mm, "end": v(-177.3, 280.63) * mm});
            skArc(sketch, "E354", {"start": v(-177.3, 280.63) * mm, "mid": v(-176.96, 279.49) * mm, "end": v(-176.05, 278.7) * mm});
            skLineSegment(sketch, "E355", {"start": v(-180.1, 257.11) * mm, "end": v(-179.41, 256.72) * mm});
            skLineSegment(sketch, "E356", {"start": v(-180.1, 257.11) * mm, "end": v(-179.41, 257.5) * mm});
            skLineSegment(sketch, "E357", {"start": v(-173.85, 258.93) * mm, "end": v(-174.54, 258.53) * mm});
            skLineSegment(sketch, "E358", {"start": v(-173.85, 258.93) * mm, "end": v(-174.54, 259.32) * mm});
            skLineSegment(sketch, "E359", {"start": v(-180.1, 257.11) * mm, "end": v(-173.85, 258.93) * mm});
            skLineSegment(sketch, "E360", {"start": v(-179.41, 256.72) * mm, "end": v(-174.54, 258.53) * mm});
            skLineSegment(sketch, "E361", {"start": v(-179.41, 257.5) * mm, "end": v(-174.54, 259.32) * mm});
            skLineSegment(sketch, "E362", {"start": v(-179.41, 256.72) * mm, "end": v(-179.41, 217.5) * mm});
            skLineSegment(sketch, "E363", {"start": v(-174.54, 258.53) * mm, "end": v(-174.54, 217.5) * mm});
            skLineSegment(sketch, "E364", {"start": v(-148.02, 412.03) * mm, "end": v(-148.02, 438.03) * mm});
            skLineSegment(sketch, "E365", {"start": v(187, 413.37) * mm, "end": v(187, 438.03) * mm});
            skLineSegment(sketch, "E366", {"start": v(-234.68, 434.85) * mm, "end": v(273.7, 434.85) * mm});
            skLineSegment(sketch, "E367", {"start": v(100.58, -60.7) * mm, "end": v(103.63, -60.7) * mm});
            skLineSegment(sketch, "E368", {"start": v(103.63, -60.7) * mm, "end": v(103.63, -75.11) * mm});
            skLineSegment(sketch, "E369", {"start": v(100.58, -60.7) * mm, "end": v(100.58, -75.11) * mm});
            skLineSegment(sketch, "E370", {"start": v(99, -79.75) * mm, "end": v(49, -79.75) * mm});
            skLineSegment(sketch, "E371", {"start": v(99, -76.7) * mm, "end": v(49, -76.7) * mm});
            skArc(sketch, "E372", {"start": v(48.23, -75.94) * mm, "mid": v(48.45, -76.48) * mm, "end": v(49, -76.7) * mm});
            skArc(sketch, "E373", {"start": v(45.18, -75.94) * mm, "mid": v(46.3, -78.63) * mm, "end": v(49, -79.75) * mm});
            skArc(sketch, "E374", {"start": v(99, -76.7) * mm, "mid": v(100.11, -76.23) * mm, "end": v(100.58, -75.11) * mm});
            skArc(sketch, "E375", {"start": v(99, -79.75) * mm, "mid": v(102.27, -78.39) * mm, "end": v(103.63, -75.11) * mm});
            skLineSegment(sketch, "E376", {"start": v(-10.55, -60.7) * mm, "end": v(-13.6, -60.7) * mm});
            skLineSegment(sketch, "E377", {"start": v(-13.6, -60.7) * mm, "end": v(-13.6, -75.11) * mm});
            skLineSegment(sketch, "E378", {"start": v(-10.55, -60.7) * mm, "end": v(-10.55, -75.11) * mm});
            skLineSegment(sketch, "E379", {"start": v(-8.96, -79.75) * mm, "end": v(40.73, -79.75) * mm});
            skLineSegment(sketch, "E380", {"start": v(-8.96, -76.7) * mm, "end": v(40.73, -76.7) * mm});
            skArc(sketch, "E381", {"start": v(40.73, -76.7) * mm, "mid": v(41.27, -76.48) * mm, "end": v(41.5, -75.94) * mm});
            skArc(sketch, "E382", {"start": v(40.73, -79.75) * mm, "mid": v(43.43, -78.63) * mm, "end": v(44.54, -75.94) * mm});
            skArc(sketch, "E383", {"start": v(-10.55, -75.11) * mm, "mid": v(-10.08, -76.23) * mm, "end": v(-8.96, -76.7) * mm});
            skArc(sketch, "E384", {"start": v(-13.6, -75.11) * mm, "mid": v(-12.24, -78.39) * mm, "end": v(-8.96, -79.75) * mm});
            skLineSegment(sketch, "E385", {"start": v(49.63, -162.09) * mm, "end": v(187.74, -162.09) * mm});
            skLineSegment(sketch, "E386", {"start": v(187.74, -86.69) * mm, "end": v(49.63, -86.69) * mm});
            skLineSegment(sketch, "E387", {"start": v(49.63, -87.49) * mm, "end": v(187.74, -87.49) * mm});
            skLineSegment(sketch, "E388", {"start": v(187.74, -162.89) * mm, "end": v(49.63, -162.89) * mm});
            skLineSegment(sketch, "E389", {"start": v(49.63, -162.89) * mm, "end": v(49.63, -86.69) * mm});
            skLineSegment(sketch, "E390", {"start": v(40.1, -162.09) * mm, "end": v(-105.22, -162.09) * mm});
            skLineSegment(sketch, "E391", {"start": v(-105.22, -86.69) * mm, "end": v(40.1, -86.69) * mm});
            skLineSegment(sketch, "E392", {"start": v(40.1, -87.49) * mm, "end": v(-105.22, -87.49) * mm});
            skLineSegment(sketch, "E393", {"start": v(-105.22, -162.89) * mm, "end": v(40.1, -162.89) * mm});
            skLineSegment(sketch, "E394", {"start": v(40.1, -162.89) * mm, "end": v(40.1, -86.69) * mm});
            skLineSegment(sketch, "E395", {"start": v(-105.22, -164.71) * mm, "end": v(-105.22, -120.76) * mm});
            skLineSegment(sketch, "E396", {"start": v(-105.22, -115.81) * mm, "end": v(-105.22, -84.15) * mm});
            skLineSegment(sketch, "E397", {"start": v(-105.22, -120.76) * mm, "end": v(-94.08, -118.26) * mm});
            skLineSegment(sketch, "E398", {"start": v(-117.4, -118.26) * mm, "end": v(-105.22, -115.81) * mm});
            skLineSegment(sketch, "E399", {"start": v(-117.4, -118.26) * mm, "end": v(-94.08, -118.26) * mm});
            skLineSegment(sketch, "E400", {"start": v(187.74, -164.71) * mm, "end": v(187.74, -120.76) * mm});
            skLineSegment(sketch, "E401", {"start": v(187.74, -115.81) * mm, "end": v(187.74, -84.15) * mm});
            skLineSegment(sketch, "E402", {"start": v(187.74, -120.76) * mm, "end": v(198.88, -118.26) * mm});
            skLineSegment(sketch, "E403", {"start": v(175.56, -118.26) * mm, "end": v(187.74, -115.81) * mm});
            skLineSegment(sketch, "E404", {"start": v(175.56, -118.26) * mm, "end": v(198.88, -118.26) * mm});
            skLineSegment(sketch, "E405", {"start": v(-19.05, -169.3) * mm, "end": v(108.77, -169.3) * mm});
            skLineSegment(sketch, "E406", {"start": v(-18.84, -167.77) * mm, "end": v(108.57, -167.77) * mm});
            skLineSegment(sketch, "E407", {"start": v(108.57, -167.77) * mm, "end": v(119.2, -164.92) * mm});
            skLineSegment(sketch, "E408", {"start": v(108.77, -169.3) * mm, "end": v(119.6, -166.4) * mm});
            skLineSegment(sketch, "E409", {"start": v(-18.84, -167.77) * mm, "end": v(-29.47, -164.92) * mm});
            skLineSegment(sketch, "E410", {"start": v(-19.05, -169.3) * mm, "end": v(-29.87, -166.4) * mm});
            skLineSegment(sketch, "E411", {"start": v(-18.84, -81.48) * mm, "end": v(108.56, -81.48) * mm});
            skLineSegment(sketch, "E412", {"start": v(-18.64, -83) * mm, "end": v(108.36, -83) * mm});
            skLineSegment(sketch, "E413", {"start": v(108.36, -83) * mm, "end": v(119.16, -83) * mm});
            skLineSegment(sketch, "E414", {"start": v(108.16, -81.48) * mm, "end": v(119.16, -81.48) * mm});
            skLineSegment(sketch, "E415", {"start": v(-18.64, -83) * mm, "end": v(-29.43, -83) * mm});
            skLineSegment(sketch, "E416", {"start": v(-18.43, -81.48) * mm, "end": v(-29.43, -81.48) * mm});
            skLineSegment(sketch, "E417", {"start": v(187.74, -130.36) * mm, "end": v(49.63, -130.36) * mm});
            skLineSegment(sketch, "E418", {"start": v(40.1, -130.36) * mm, "end": v(-105.22, -130.36) * mm});
            skLineSegment(sketch, "E419", {"start": v(187.74, -131.16) * mm, "end": v(49.63, -131.16) * mm});
            skLineSegment(sketch, "E420", {"start": v(40.1, -131.16) * mm, "end": v(-105.22, -131.16) * mm});
            skLineSegment(sketch, "E421", {"start": v(50.63, -132.01) * mm, "end": v(152.23, -132.01) * mm});
            skLineSegment(sketch, "E422", {"start": v(50.63, -134.28) * mm, "end": v(152.23, -134.28) * mm});
            skLineSegment(sketch, "E423", {"start": v(50.63, -134.85) * mm, "end": v(152.23, -134.85) * mm});
            skLineSegment(sketch, "E424", {"start": v(50.63, -132.01) * mm, "end": v(50.63, -134.85) * mm});
            skLineSegment(sketch, "E425", {"start": v(152.23, -132.01) * mm, "end": v(152.23, -134.85) * mm});
            skLineSegment(sketch, "E426", {"start": v(-62.42, -132.01) * mm, "end": v(39.18, -132.01) * mm});
            skLineSegment(sketch, "E427", {"start": v(-62.42, -134.28) * mm, "end": v(39.18, -134.28) * mm});
            skLineSegment(sketch, "E428", {"start": v(-62.42, -134.85) * mm, "end": v(39.18, -134.85) * mm});
            skLineSegment(sketch, "E429", {"start": v(-62.42, -132.01) * mm, "end": v(-62.42, -134.85) * mm});
            skLineSegment(sketch, "E430", {"start": v(39.18, -132.01) * mm, "end": v(39.18, -134.85) * mm});
            skLineSegment(sketch, "E431", {"start": v(22.26, -136.63) * mm, "end": v(22.26, -135.36) * mm});
            skLineSegment(sketch, "E432", {"start": v(9.05, -136.63) * mm, "end": v(9.05, -135.36) * mm});
            skLineSegment(sketch, "E433", {"start": v(20.85, -141.05) * mm, "end": v(20.85, -136.63) * mm});
            skLineSegment(sketch, "E434", {"start": v(10.46, -141.05) * mm, "end": v(10.46, -136.63) * mm});
            skLineSegment(sketch, "E435", {"start": v(18.1, -93.54) * mm, "end": v(18.1, -92.52) * mm});
            skLineSegment(sketch, "E436", {"start": v(18.1, -91.73) * mm, "end": v(18.1, -90.7) * mm});
            skLineSegment(sketch, "E437", {"start": v(18.1, -89.92) * mm, "end": v(18.1, -88.9) * mm});
            skLineSegment(sketch, "E438", {"start": v(18.1, -88.1) * mm, "end": v(18.1, -87.08) * mm});
            skLineSegment(sketch, "E439", {"start": v(18.1, -86.3) * mm, "end": v(18.1, -85.27) * mm});
            skLineSegment(sketch, "E440", {"start": v(18.1, -84.48) * mm, "end": v(18.1, -83.46) * mm});
            skLineSegment(sketch, "E441", {"start": v(18.1, -82.66) * mm, "end": v(18.1, -81.64) * mm});
            skLineSegment(sketch, "E442", {"start": v(18.1, -80.85) * mm, "end": v(18.1, -79.83) * mm});
            skLineSegment(sketch, "E443", {"start": v(18.1, -75.4) * mm, "end": v(18.1, -74.39) * mm});
            skLineSegment(sketch, "E444", {"start": v(13.22, -95.36) * mm, "end": v(13.22, -94.34) * mm});
            skLineSegment(sketch, "E445", {"start": v(13.22, -93.54) * mm, "end": v(13.22, -92.52) * mm});
            skLineSegment(sketch, "E446", {"start": v(13.22, -91.73) * mm, "end": v(13.22, -90.7) * mm});
            skLineSegment(sketch, "E447", {"start": v(13.22, -89.92) * mm, "end": v(13.22, -88.9) * mm});
            skLineSegment(sketch, "E448", {"start": v(13.22, -88.1) * mm, "end": v(13.22, -87.08) * mm});
            skLineSegment(sketch, "E449", {"start": v(13.22, -86.3) * mm, "end": v(13.22, -85.27) * mm});
            skLineSegment(sketch, "E450", {"start": v(13.22, -84.48) * mm, "end": v(13.22, -83.46) * mm});
            skLineSegment(sketch, "E451", {"start": v(13.22, -82.66) * mm, "end": v(13.22, -81.64) * mm});
            skLineSegment(sketch, "E452", {"start": v(13.22, -80.85) * mm, "end": v(13.22, -79.83) * mm});
            skLineSegment(sketch, "E453", {"start": v(12.53, -93.94) * mm, "end": v(13.22, -94.34) * mm});
            skLineSegment(sketch, "E454", {"start": v(12.53, -93.94) * mm, "end": v(13.22, -93.54) * mm});
            skLineSegment(sketch, "E455", {"start": v(12.53, -92.13) * mm, "end": v(13.22, -92.52) * mm});
            skLineSegment(sketch, "E456", {"start": v(12.53, -92.13) * mm, "end": v(13.22, -91.73) * mm});
            skLineSegment(sketch, "E457", {"start": v(18.78, -92.13) * mm, "end": v(18.1, -92.52) * mm});
            skLineSegment(sketch, "E458", {"start": v(18.78, -92.13) * mm, "end": v(18.1, -91.73) * mm});
            skLineSegment(sketch, "E459", {"start": v(18.78, -90.31) * mm, "end": v(18.1, -90.7) * mm});
            skLineSegment(sketch, "E460", {"start": v(18.78, -90.31) * mm, "end": v(18.1, -89.92) * mm});
            skLineSegment(sketch, "E461", {"start": v(12.53, -93.94) * mm, "end": v(18.78, -92.13) * mm});
            skLineSegment(sketch, "E462", {"start": v(12.53, -92.13) * mm, "end": v(18.78, -90.31) * mm});
            skLineSegment(sketch, "E463", {"start": v(13.22, -94.34) * mm, "end": v(18.1, -92.52) * mm});
            skLineSegment(sketch, "E464", {"start": v(13.22, -93.54) * mm, "end": v(18.1, -91.73) * mm});
            skLineSegment(sketch, "E465", {"start": v(13.22, -92.52) * mm, "end": v(18.1, -90.7) * mm});
            skLineSegment(sketch, "E466", {"start": v(13.22, -91.73) * mm, "end": v(18.1, -89.92) * mm});
            skLineSegment(sketch, "E467", {"start": v(12.53, -90.31) * mm, "end": v(13.22, -90.7) * mm});
            skLineSegment(sketch, "E468", {"start": v(12.53, -90.31) * mm, "end": v(13.22, -89.92) * mm});
            skLineSegment(sketch, "E469", {"start": v(12.53, -88.5) * mm, "end": v(13.22, -88.9) * mm});
            skLineSegment(sketch, "E470", {"start": v(12.53, -88.5) * mm, "end": v(13.22, -88.1) * mm});
            skLineSegment(sketch, "E471", {"start": v(18.78, -88.5) * mm, "end": v(18.1, -88.9) * mm});
            skLineSegment(sketch, "E472", {"start": v(18.78, -88.5) * mm, "end": v(18.1, -88.1) * mm});
            skLineSegment(sketch, "E473", {"start": v(18.78, -86.69) * mm, "end": v(18.1, -87.08) * mm});
            skLineSegment(sketch, "E474", {"start": v(18.78, -86.69) * mm, "end": v(18.1, -86.3) * mm});
            skLineSegment(sketch, "E475", {"start": v(12.53, -90.31) * mm, "end": v(18.78, -88.5) * mm});
            skLineSegment(sketch, "E476", {"start": v(12.53, -88.5) * mm, "end": v(18.78, -86.69) * mm});
            skLineSegment(sketch, "E477", {"start": v(13.22, -90.7) * mm, "end": v(18.1, -88.9) * mm});
            skLineSegment(sketch, "E478", {"start": v(13.22, -89.92) * mm, "end": v(18.1, -88.1) * mm});
            skLineSegment(sketch, "E479", {"start": v(13.22, -88.9) * mm, "end": v(18.1, -87.08) * mm});
            skLineSegment(sketch, "E480", {"start": v(13.22, -88.1) * mm, "end": v(18.1, -86.3) * mm});
            skLineSegment(sketch, "E481", {"start": v(12.53, -86.69) * mm, "end": v(13.22, -87.08) * mm});
            skLineSegment(sketch, "E482", {"start": v(12.53, -86.69) * mm, "end": v(13.22, -86.3) * mm});
            skLineSegment(sketch, "E483", {"start": v(18.78, -84.87) * mm, "end": v(18.1, -85.27) * mm});
            skLineSegment(sketch, "E484", {"start": v(18.78, -84.87) * mm, "end": v(18.1, -84.48) * mm});
            skLineSegment(sketch, "E485", {"start": v(12.53, -86.69) * mm, "end": v(18.78, -84.87) * mm});
            skLineSegment(sketch, "E486", {"start": v(13.22, -87.08) * mm, "end": v(18.1, -85.27) * mm});
            skLineSegment(sketch, "E487", {"start": v(13.22, -86.3) * mm, "end": v(18.1, -84.48) * mm});
            skLineSegment(sketch, "E488", {"start": v(12.53, -84.87) * mm, "end": v(13.22, -85.27) * mm});
            skLineSegment(sketch, "E489", {"start": v(12.53, -84.87) * mm, "end": v(13.22, -84.48) * mm});
            skLineSegment(sketch, "E490", {"start": v(12.53, -83.06) * mm, "end": v(13.22, -83.46) * mm});
            skLineSegment(sketch, "E491", {"start": v(12.53, -83.06) * mm, "end": v(13.22, -82.66) * mm});
            skLineSegment(sketch, "E492", {"start": v(18.78, -83.06) * mm, "end": v(18.1, -83.46) * mm});
            skLineSegment(sketch, "E493", {"start": v(18.78, -83.06) * mm, "end": v(18.1, -82.66) * mm});
            skLineSegment(sketch, "E494", {"start": v(18.78, -81.25) * mm, "end": v(18.1, -81.64) * mm});
            skLineSegment(sketch, "E495", {"start": v(18.78, -81.25) * mm, "end": v(18.1, -80.85) * mm});
            skLineSegment(sketch, "E496", {"start": v(12.53, -84.87) * mm, "end": v(18.78, -83.06) * mm});
            skLineSegment(sketch, "E497", {"start": v(12.53, -83.06) * mm, "end": v(18.78, -81.25) * mm});
            skLineSegment(sketch, "E498", {"start": v(13.22, -85.27) * mm, "end": v(18.1, -83.46) * mm});
            skLineSegment(sketch, "E499", {"start": v(13.22, -84.48) * mm, "end": v(18.1, -82.66) * mm});
            skLineSegment(sketch, "E500", {"start": v(13.22, -83.46) * mm, "end": v(18.1, -81.64) * mm});
            skLineSegment(sketch, "E501", {"start": v(13.22, -82.66) * mm, "end": v(18.1, -80.85) * mm});
            skLineSegment(sketch, "E502", {"start": v(12.53, -81.25) * mm, "end": v(13.22, -81.64) * mm});
            skLineSegment(sketch, "E503", {"start": v(12.53, -81.25) * mm, "end": v(13.22, -80.85) * mm});
            skLineSegment(sketch, "E504", {"start": v(13.22, -81.64) * mm, "end": v(18.1, -79.83) * mm});
            skLineSegment(sketch, "E505", {"start": v(12.53, -75.8) * mm, "end": v(13.22, -76.2) * mm});
            skLineSegment(sketch, "E506", {"start": v(12.53, -75.8) * mm, "end": v(13.22, -75.4) * mm});
            skLineSegment(sketch, "E507", {"start": v(18.78, -75.8) * mm, "end": v(18.1, -76.2) * mm});
            skLineSegment(sketch, "E508", {"start": v(18.78, -75.8) * mm, "end": v(18.1, -75.4) * mm});
            skLineSegment(sketch, "E509", {"start": v(18.78, -74) * mm, "end": v(18.1, -74.39) * mm});
            skLineSegment(sketch, "E510", {"start": v(18.78, -74) * mm, "end": v(18.1, -73.6) * mm});
            skLineSegment(sketch, "E511", {"start": v(9.05, -135.36) * mm, "end": v(22.26, -135.36) * mm});
            skLineSegment(sketch, "E512", {"start": v(9.05, -136.63) * mm, "end": v(22.26, -136.63) * mm});
            skLineSegment(sketch, "E513", {"start": v(11.15, -141.45) * mm, "end": v(20.15, -141.45) * mm});
            skLineSegment(sketch, "E514", {"start": v(13.06, -141.05) * mm, "end": v(13.06, -136.63) * mm});
            skLineSegment(sketch, "E515", {"start": v(18.25, -141.05) * mm, "end": v(18.25, -136.63) * mm});
            skLineSegment(sketch, "E516", {"start": v(11.15, -141.45) * mm, "end": v(10.46, -141.05) * mm});
            skLineSegment(sketch, "E517", {"start": v(20.15, -141.45) * mm, "end": v(20.85, -141.05) * mm});
            skLineSegment(sketch, "E518", {"start": v(17.55, -141.45) * mm, "end": v(18.25, -141.05) * mm});
            skLineSegment(sketch, "E519", {"start": v(12.36, -141.45) * mm, "end": v(13.06, -141.05) * mm});
            skLineSegment(sketch, "E520", {"start": v(18.95, -141.45) * mm, "end": v(18.25, -141.05) * mm});
            skLineSegment(sketch, "E521", {"start": v(13.75, -141.45) * mm, "end": v(13.06, -141.05) * mm});
            skLineSegment(sketch, "E522", {"start": v(13.22, -75.4) * mm, "end": v(13.22, -63.93) * mm});
            skLineSegment(sketch, "E523", {"start": v(17.44, -73.84) * mm, "end": v(17.44, -63.93) * mm});
            skLineSegment(sketch, "E524", {"start": v(15.33, -62.7) * mm, "end": v(13.22, -63.93) * mm});
            skLineSegment(sketch, "E525", {"start": v(15.33, -62.7) * mm, "end": v(17.44, -63.93) * mm});
            skLineSegment(sketch, "E526", {"start": v(15.33, -62.7) * mm, "end": v(15.33, -72.23) * mm});
            skLineSegment(sketch, "E527", {"start": v(12.53, -95.75) * mm, "end": v(13.22, -96.15) * mm});
            skLineSegment(sketch, "E528", {"start": v(12.53, -95.75) * mm, "end": v(13.22, -95.36) * mm});
            skLineSegment(sketch, "E529", {"start": v(18.78, -93.94) * mm, "end": v(18.1, -94.34) * mm});
            skLineSegment(sketch, "E530", {"start": v(18.78, -93.94) * mm, "end": v(18.1, -93.54) * mm});
            skLineSegment(sketch, "E531", {"start": v(12.53, -95.75) * mm, "end": v(18.78, -93.94) * mm});
            skLineSegment(sketch, "E532", {"start": v(13.22, -96.15) * mm, "end": v(18.1, -94.34) * mm});
            skLineSegment(sketch, "E533", {"start": v(13.22, -95.36) * mm, "end": v(18.1, -93.54) * mm});
            skLineSegment(sketch, "E534", {"start": v(13.22, -96.15) * mm, "end": v(13.22, -135.36) * mm});
            skLineSegment(sketch, "E535", {"start": v(18.1, -94.34) * mm, "end": v(18.1, -135.36) * mm});
            skLineSegment(sketch, "E536", {"start": v(-29.43, -83) * mm, "end": v(-29.43, -81.48) * mm});
            skLineSegment(sketch, "E537", {"start": v(119.16, -83) * mm, "end": v(119.16, -81.48) * mm});
            skLineSegment(sketch, "E538", {"start": v(119.2, -164.92) * mm, "end": v(119.6, -166.4) * mm});
            skLineSegment(sketch, "E539", {"start": v(-29.87, -166.4) * mm, "end": v(-29.47, -164.92) * mm});
            skLineSegment(sketch, "E540", {"start": v(-29.16, -165.55) * mm, "end": v(2.6, -165.55) * mm});
            skLineSegment(sketch, "E541", {"start": v(-29.16, -164.03) * mm, "end": v(2.6, -164.03) * mm});
            skLineSegment(sketch, "E542", {"start": v(-29.16, -164.03) * mm, "end": v(-29.16, -165.55) * mm});
            skLineSegment(sketch, "E543", {"start": v(2.6, -164.03) * mm, "end": v(2.6, -165.55) * mm});
            skLineSegment(sketch, "E544", {"start": v(87.33, -165.55) * mm, "end": v(119.08, -165.55) * mm});
            skLineSegment(sketch, "E545", {"start": v(87.33, -164.03) * mm, "end": v(119.08, -164.03) * mm});
            skLineSegment(sketch, "E546", {"start": v(87.33, -164.03) * mm, "end": v(87.33, -165.55) * mm});
            skLineSegment(sketch, "E547", {"start": v(119.08, -164.03) * mm, "end": v(119.08, -165.55) * mm});
            skLineSegment(sketch, "E548", {"start": v(-4.94, -85.56) * mm, "end": v(34.87, -85.56) * mm});
            skLineSegment(sketch, "E549", {"start": v(-4.94, -84.04) * mm, "end": v(34.87, -84.04) * mm});
            skLineSegment(sketch, "E550", {"start": v(-4.94, -84.04) * mm, "end": v(-4.94, -85.56) * mm});
            skLineSegment(sketch, "E551", {"start": v(34.87, -84.04) * mm, "end": v(34.87, -85.56) * mm});
            skLineSegment(sketch, "E552", {"start": v(55.88, -85.56) * mm, "end": v(94.6, -85.56) * mm});
            skLineSegment(sketch, "E553", {"start": v(55.88, -84.04) * mm, "end": v(94.6, -84.04) * mm});
            skLineSegment(sketch, "E554", {"start": v(55.88, -84.04) * mm, "end": v(55.88, -85.56) * mm});
            skLineSegment(sketch, "E555", {"start": v(94.6, -84.04) * mm, "end": v(94.6, -85.56) * mm});
            skLineSegment(sketch, "E556", {"start": v(-5.7, -170.24) * mm, "end": v(-17.48, -170.24) * mm});
            skLineSegment(sketch, "E557", {"start": v(-14.28, -168.36) * mm, "end": v(-8.9, -166.58) * mm});
            skLineSegment(sketch, "E558", {"start": v(-14.28, -168.36) * mm, "end": v(-13.6, -168.75) * mm});
            skLineSegment(sketch, "E559", {"start": v(-14.28, -168.36) * mm, "end": v(-13.6, -167.97) * mm});
            skLineSegment(sketch, "E560", {"start": v(-8.9, -166.58) * mm, "end": v(-9.58, -166.19) * mm});
            skLineSegment(sketch, "E561", {"start": v(-8.9, -166.58) * mm, "end": v(-9.58, -166.97) * mm});
            skLineSegment(sketch, "E562", {"start": v(-9.58, -166.19) * mm, "end": v(-13.6, -167.97) * mm});
            skLineSegment(sketch, "E563", {"start": v(-13.6, -168.75) * mm, "end": v(-9.58, -166.97) * mm});
            skLineSegment(sketch, "E564", {"start": v(-8.9, -164.8) * mm, "end": v(-9.58, -164.4) * mm});
            skLineSegment(sketch, "E565", {"start": v(-8.9, -164.8) * mm, "end": v(-9.58, -165.2) * mm});
            skLineSegment(sketch, "E566", {"start": v(-14.28, -166.58) * mm, "end": v(-8.9, -164.8) * mm});
            skLineSegment(sketch, "E567", {"start": v(-9.58, -164.4) * mm, "end": v(-13.6, -166.19) * mm});
            skLineSegment(sketch, "E568", {"start": v(-13.6, -166.97) * mm, "end": v(-9.58, -165.2) * mm});
            skLineSegment(sketch, "E569", {"start": v(-14.28, -166.58) * mm, "end": v(-13.6, -166.97) * mm});
            skLineSegment(sketch, "E570", {"start": v(-14.28, -166.58) * mm, "end": v(-13.6, -166.19) * mm});
            skLineSegment(sketch, "E571", {"start": v(-8.9, -163.02) * mm, "end": v(-9.58, -162.63) * mm});
            skLineSegment(sketch, "E572", {"start": v(-8.9, -163.02) * mm, "end": v(-9.58, -163.42) * mm});
            skLineSegment(sketch, "E573", {"start": v(-14.28, -164.8) * mm, "end": v(-8.9, -163.02) * mm});
            skLineSegment(sketch, "E574", {"start": v(-9.58, -162.63) * mm, "end": v(-13.6, -164.4) * mm});
            skLineSegment(sketch, "E575", {"start": v(-13.6, -165.2) * mm, "end": v(-9.58, -163.42) * mm});
            skLineSegment(sketch, "E576", {"start": v(-14.28, -164.8) * mm, "end": v(-13.6, -165.2) * mm});
            skLineSegment(sketch, "E577", {"start": v(-14.28, -164.8) * mm, "end": v(-13.6, -164.4) * mm});
            skLineSegment(sketch, "E578", {"start": v(-8.9, -161.24) * mm, "end": v(-9.58, -160.85) * mm});
            skLineSegment(sketch, "E579", {"start": v(-8.9, -161.24) * mm, "end": v(-9.58, -161.64) * mm});
            skLineSegment(sketch, "E580", {"start": v(-14.28, -163.02) * mm, "end": v(-8.9, -161.24) * mm});
            skLineSegment(sketch, "E581", {"start": v(-9.58, -160.85) * mm, "end": v(-13.6, -162.63) * mm});
            skLineSegment(sketch, "E582", {"start": v(-13.6, -163.42) * mm, "end": v(-9.58, -161.64) * mm});
            skLineSegment(sketch, "E583", {"start": v(-14.28, -163.02) * mm, "end": v(-13.6, -163.42) * mm});
            skLineSegment(sketch, "E584", {"start": v(-14.28, -163.02) * mm, "end": v(-13.6, -162.63) * mm});
            skLineSegment(sketch, "E585", {"start": v(-8.9, -159.46) * mm, "end": v(-9.58, -159.07) * mm});
            skLineSegment(sketch, "E586", {"start": v(-8.9, -159.46) * mm, "end": v(-9.58, -159.86) * mm});
            skLineSegment(sketch, "E587", {"start": v(-14.28, -161.24) * mm, "end": v(-8.9, -159.46) * mm});
            skLineSegment(sketch, "E588", {"start": v(-9.58, -159.07) * mm, "end": v(-13.6, -160.85) * mm});
            skLineSegment(sketch, "E589", {"start": v(-13.6, -161.64) * mm, "end": v(-9.58, -159.86) * mm});
            skLineSegment(sketch, "E590", {"start": v(-14.28, -161.24) * mm, "end": v(-13.6, -161.64) * mm});
            skLineSegment(sketch, "E591", {"start": v(-14.28, -161.24) * mm, "end": v(-13.6, -160.85) * mm});
            skLineSegment(sketch, "E592", {"start": v(-8.9, -157.68) * mm, "end": v(-9.58, -157.29) * mm});
            skLineSegment(sketch, "E593", {"start": v(-8.9, -157.68) * mm, "end": v(-9.58, -158.08) * mm});
            skLineSegment(sketch, "E594", {"start": v(-14.28, -159.46) * mm, "end": v(-8.9, -157.68) * mm});
            skLineSegment(sketch, "E595", {"start": v(-9.58, -157.29) * mm, "end": v(-13.6, -159.07) * mm});
            skLineSegment(sketch, "E596", {"start": v(-13.6, -159.86) * mm, "end": v(-9.58, -158.08) * mm});
            skLineSegment(sketch, "E597", {"start": v(-14.28, -159.46) * mm, "end": v(-13.6, -159.86) * mm});
            skLineSegment(sketch, "E598", {"start": v(-14.28, -159.46) * mm, "end": v(-13.6, -159.07) * mm});
            skLineSegment(sketch, "E599", {"start": v(-14.28, -157.68) * mm, "end": v(-11.6, -157.19) * mm});
            skLineSegment(sketch, "E600", {"start": v(-11.6, -157.19) * mm, "end": v(-13.6, -157.29) * mm});
            skLineSegment(sketch, "E601", {"start": v(-13.6, -158.08) * mm, "end": v(-11.6, -157.19) * mm});
            skLineSegment(sketch, "E602", {"start": v(-14.28, -157.68) * mm, "end": v(-13.6, -158.08) * mm});
            skLineSegment(sketch, "E603", {"start": v(-14.28, -157.68) * mm, "end": v(-13.6, -157.29) * mm});
            skLineSegment(sketch, "E604", {"start": v(-13.6, -158.08) * mm, "end": v(-13.6, -159.07) * mm});
            skLineSegment(sketch, "E605", {"start": v(-9.58, -158.08) * mm, "end": v(-9.58, -159.07) * mm});
            skLineSegment(sketch, "E606", {"start": v(-9.58, -159.86) * mm, "end": v(-9.58, -160.85) * mm});
            skLineSegment(sketch, "E607", {"start": v(-9.58, -161.64) * mm, "end": v(-9.58, -162.63) * mm});
            skLineSegment(sketch, "E608", {"start": v(-9.58, -163.42) * mm, "end": v(-9.58, -164.4) * mm});
            skLineSegment(sketch, "E609", {"start": v(-9.58, -165.2) * mm, "end": v(-9.58, -166.19) * mm});
            skLineSegment(sketch, "E610", {"start": v(-9.58, -166.97) * mm, "end": v(-9.58, -167.97) * mm});
            skLineSegment(sketch, "E611", {"start": v(-9.58, -168.75) * mm, "end": v(-9.58, -170.24) * mm});
            skLineSegment(sketch, "E612", {"start": v(-13.6, -168.75) * mm, "end": v(-13.6, -169.74) * mm});
            skLineSegment(sketch, "E613", {"start": v(-13.6, -166.97) * mm, "end": v(-13.6, -167.97) * mm});
            skLineSegment(sketch, "E614", {"start": v(-13.6, -165.2) * mm, "end": v(-13.6, -166.19) * mm});
            skLineSegment(sketch, "E615", {"start": v(-13.6, -163.42) * mm, "end": v(-13.6, -164.4) * mm});
            skLineSegment(sketch, "E616", {"start": v(-13.6, -161.64) * mm, "end": v(-13.6, -162.63) * mm});
            skLineSegment(sketch, "E617", {"start": v(-13.6, -159.86) * mm, "end": v(-13.6, -160.85) * mm});
            skLineSegment(sketch, "E618", {"start": v(-8.9, -168.36) * mm, "end": v(-9.58, -167.97) * mm});
            skLineSegment(sketch, "E619", {"start": v(-8.9, -168.36) * mm, "end": v(-9.58, -168.75) * mm});
            skLineSegment(sketch, "E620", {"start": v(-14.28, -170.14) * mm, "end": v(-8.9, -168.36) * mm});
            skLineSegment(sketch, "E621", {"start": v(-9.58, -167.97) * mm, "end": v(-13.6, -169.74) * mm});
            skLineSegment(sketch, "E622", {"start": v(-12.93, -170.24) * mm, "end": v(-9.58, -168.75) * mm});
            skLineSegment(sketch, "E623", {"start": v(-14.28, -170.14) * mm, "end": v(-13.6, -169.74) * mm});
            skLineSegment(sketch, "E624", {"start": v(-14.28, -170.14) * mm, "end": v(-14.11, -170.24) * mm});
            skLineSegment(sketch, "E625", {"start": v(-5.7, -171.12) * mm, "end": v(-17.48, -171.12) * mm});
            skLineSegment(sketch, "E626", {"start": v(-17.48, -170.24) * mm, "end": v(-17.48, -171.12) * mm});
            skLineSegment(sketch, "E627", {"start": v(-5.7, -170.24) * mm, "end": v(-5.7, -171.12) * mm});
            skLineSegment(sketch, "E628", {"start": v(-7.92, -174.54) * mm, "end": v(-15.33, -174.54) * mm});
            skLineSegment(sketch, "E629", {"start": v(-6.75, -171.12) * mm, "end": v(-6.75, -173.47) * mm});
            skLineSegment(sketch, "E630", {"start": v(-16.43, -171.12) * mm, "end": v(-16.43, -173.47) * mm});
            skLineSegment(sketch, "E631", {"start": v(-14.16, -173.47) * mm, "end": v(-14.16, -171.12) * mm});
            skLineSegment(sketch, "E632", {"start": v(-9.03, -173.47) * mm, "end": v(-9.03, -171.12) * mm});
            skArc(sketch, "E633", {"start": v(-14.16, -173.47) * mm, "mid": v(-11.6, -174.54) * mm, "end": v(-9.03, -173.47) * mm});
            skArc(sketch, "E634", {"start": v(-9.03, -173.47) * mm, "mid": v(-7.89, -174.54) * mm, "end": v(-6.75, -173.47) * mm});
            skArc(sketch, "E635", {"start": v(-16.43, -173.47) * mm, "mid": v(-15.3, -174.54) * mm, "end": v(-14.16, -173.47) * mm});
            skLineSegment(sketch, "E636", {"start": v(-13.6, -157.29) * mm, "end": v(-13.6, -152.35) * mm});
            skLineSegment(sketch, "E637", {"start": v(-9.58, -157.29) * mm, "end": v(-9.58, -152.35) * mm});
            skLineSegment(sketch, "E638", {"start": v(-11.6, -151.19) * mm, "end": v(-13.6, -152.35) * mm});
            skLineSegment(sketch, "E639", {"start": v(-11.6, -151.19) * mm, "end": v(-9.58, -152.35) * mm});
            skLineSegment(sketch, "E640", {"start": v(-11.6, -151.19) * mm, "end": v(-11.6, -153.73) * mm});
            skArc(sketch, "E641", {"start": v(-11.6, -153.73) * mm, "mid": v(-11, -155.15) * mm, "end": v(-9.58, -155.74) * mm});
            skLineSegment(sketch, "E642", {"start": v(107.15, -170.24) * mm, "end": v(95.36, -170.24) * mm});
            skLineSegment(sketch, "E643", {"start": v(98.56, -168.36) * mm, "end": v(103.94, -166.58) * mm});
            skLineSegment(sketch, "E644", {"start": v(98.56, -168.36) * mm, "end": v(99.24, -168.75) * mm});
            skLineSegment(sketch, "E645", {"start": v(98.56, -168.36) * mm, "end": v(99.24, -167.97) * mm});
            skLineSegment(sketch, "E646", {"start": v(103.94, -166.58) * mm, "end": v(103.26, -166.19) * mm});
            skLineSegment(sketch, "E647", {"start": v(103.94, -166.58) * mm, "end": v(103.26, -166.97) * mm});
            skLineSegment(sketch, "E648", {"start": v(103.26, -166.19) * mm, "end": v(99.24, -167.97) * mm});
            skLineSegment(sketch, "E649", {"start": v(99.24, -168.75) * mm, "end": v(103.26, -166.97) * mm});
            skLineSegment(sketch, "E650", {"start": v(103.94, -164.8) * mm, "end": v(103.26, -164.4) * mm});
            skLineSegment(sketch, "E651", {"start": v(103.94, -164.8) * mm, "end": v(103.26, -165.2) * mm});
            skLineSegment(sketch, "E652", {"start": v(98.56, -166.58) * mm, "end": v(103.94, -164.8) * mm});
            skLineSegment(sketch, "E653", {"start": v(103.26, -164.4) * mm, "end": v(99.24, -166.19) * mm});
            skLineSegment(sketch, "E654", {"start": v(99.24, -166.97) * mm, "end": v(103.26, -165.2) * mm});
            skLineSegment(sketch, "E655", {"start": v(98.56, -166.58) * mm, "end": v(99.24, -166.97) * mm});
            skLineSegment(sketch, "E656", {"start": v(98.56, -166.58) * mm, "end": v(99.24, -166.19) * mm});
            skLineSegment(sketch, "E657", {"start": v(103.94, -163.02) * mm, "end": v(103.26, -162.63) * mm});
            skLineSegment(sketch, "E658", {"start": v(103.94, -163.02) * mm, "end": v(103.26, -163.42) * mm});
            skLineSegment(sketch, "E659", {"start": v(98.56, -164.8) * mm, "end": v(103.94, -163.02) * mm});
            skLineSegment(sketch, "E660", {"start": v(103.26, -162.63) * mm, "end": v(99.24, -164.4) * mm});
            skLineSegment(sketch, "E661", {"start": v(99.24, -165.2) * mm, "end": v(103.26, -163.42) * mm});
            skLineSegment(sketch, "E662", {"start": v(98.56, -164.8) * mm, "end": v(99.24, -165.2) * mm});
            skLineSegment(sketch, "E663", {"start": v(98.56, -164.8) * mm, "end": v(99.24, -164.4) * mm});
            skLineSegment(sketch, "E664", {"start": v(103.94, -161.24) * mm, "end": v(103.26, -160.85) * mm});
            skLineSegment(sketch, "E665", {"start": v(103.94, -161.24) * mm, "end": v(103.26, -161.64) * mm});
            skLineSegment(sketch, "E666", {"start": v(98.56, -163.02) * mm, "end": v(103.94, -161.24) * mm});
            skLineSegment(sketch, "E667", {"start": v(103.26, -160.85) * mm, "end": v(99.24, -162.63) * mm});
            skLineSegment(sketch, "E668", {"start": v(99.24, -163.42) * mm, "end": v(103.26, -161.64) * mm});
            skLineSegment(sketch, "E669", {"start": v(98.56, -163.02) * mm, "end": v(99.24, -163.42) * mm});
            skLineSegment(sketch, "E670", {"start": v(98.56, -163.02) * mm, "end": v(99.24, -162.63) * mm});
            skLineSegment(sketch, "E671", {"start": v(103.94, -159.46) * mm, "end": v(103.26, -159.07) * mm});
            skLineSegment(sketch, "E672", {"start": v(103.94, -159.46) * mm, "end": v(103.26, -159.86) * mm});
            skLineSegment(sketch, "E673", {"start": v(98.56, -161.24) * mm, "end": v(103.94, -159.46) * mm});
            skLineSegment(sketch, "E674", {"start": v(103.26, -159.07) * mm, "end": v(99.24, -160.85) * mm});
            skLineSegment(sketch, "E675", {"start": v(99.24, -161.64) * mm, "end": v(103.26, -159.86) * mm});
            skLineSegment(sketch, "E676", {"start": v(98.56, -161.24) * mm, "end": v(99.24, -161.64) * mm});
            skLineSegment(sketch, "E677", {"start": v(98.56, -161.24) * mm, "end": v(99.24, -160.85) * mm});
            skLineSegment(sketch, "E678", {"start": v(103.94, -157.68) * mm, "end": v(103.26, -157.29) * mm});
            skLineSegment(sketch, "E679", {"start": v(103.94, -157.68) * mm, "end": v(103.26, -158.08) * mm});
            skLineSegment(sketch, "E680", {"start": v(98.56, -159.46) * mm, "end": v(103.94, -157.68) * mm});
            skLineSegment(sketch, "E681", {"start": v(103.26, -157.29) * mm, "end": v(99.24, -159.07) * mm});
            skLineSegment(sketch, "E682", {"start": v(99.24, -159.86) * mm, "end": v(103.26, -158.08) * mm});
            skLineSegment(sketch, "E683", {"start": v(98.56, -159.46) * mm, "end": v(99.24, -159.86) * mm});
            skLineSegment(sketch, "E684", {"start": v(98.56, -159.46) * mm, "end": v(99.24, -159.07) * mm});
            skLineSegment(sketch, "E685", {"start": v(98.56, -157.68) * mm, "end": v(101.25, -157.19) * mm});
            skLineSegment(sketch, "E686", {"start": v(101.25, -157.19) * mm, "end": v(99.24, -157.29) * mm});
            skLineSegment(sketch, "E687", {"start": v(99.24, -158.08) * mm, "end": v(101.25, -157.19) * mm});
            skLineSegment(sketch, "E688", {"start": v(98.56, -157.68) * mm, "end": v(99.24, -158.08) * mm});
            skLineSegment(sketch, "E689", {"start": v(98.56, -157.68) * mm, "end": v(99.24, -157.29) * mm});
            skLineSegment(sketch, "E690", {"start": v(99.24, -158.08) * mm, "end": v(99.24, -159.07) * mm});
            skLineSegment(sketch, "E691", {"start": v(103.26, -158.08) * mm, "end": v(103.26, -159.07) * mm});
            skLineSegment(sketch, "E692", {"start": v(103.26, -159.86) * mm, "end": v(103.26, -160.85) * mm});
            skLineSegment(sketch, "E693", {"start": v(103.26, -161.64) * mm, "end": v(103.26, -162.63) * mm});
            skLineSegment(sketch, "E694", {"start": v(103.26, -163.42) * mm, "end": v(103.26, -164.4) * mm});
            skLineSegment(sketch, "E695", {"start": v(103.26, -165.2) * mm, "end": v(103.26, -166.19) * mm});
            skLineSegment(sketch, "E696", {"start": v(103.26, -166.97) * mm, "end": v(103.26, -167.97) * mm});
            skLineSegment(sketch, "E697", {"start": v(103.26, -168.75) * mm, "end": v(103.26, -170.24) * mm});
            skLineSegment(sketch, "E698", {"start": v(99.24, -168.75) * mm, "end": v(99.24, -169.74) * mm});
            skLineSegment(sketch, "E699", {"start": v(99.24, -166.97) * mm, "end": v(99.24, -167.97) * mm});
            skLineSegment(sketch, "E700", {"start": v(99.24, -165.2) * mm, "end": v(99.24, -166.19) * mm});
            skLineSegment(sketch, "E701", {"start": v(99.24, -163.42) * mm, "end": v(99.24, -164.4) * mm});
            skLineSegment(sketch, "E702", {"start": v(99.24, -161.64) * mm, "end": v(99.24, -162.63) * mm});
            skLineSegment(sketch, "E703", {"start": v(99.24, -159.86) * mm, "end": v(99.24, -160.85) * mm});
            skLineSegment(sketch, "E704", {"start": v(103.94, -168.36) * mm, "end": v(103.26, -167.97) * mm});
            skLineSegment(sketch, "E705", {"start": v(103.94, -168.36) * mm, "end": v(103.26, -168.75) * mm});
            skLineSegment(sketch, "E706", {"start": v(98.56, -170.14) * mm, "end": v(103.94, -168.36) * mm});
            skLineSegment(sketch, "E707", {"start": v(103.26, -167.97) * mm, "end": v(99.24, -169.74) * mm});
            skLineSegment(sketch, "E708", {"start": v(99.91, -170.24) * mm, "end": v(103.26, -168.75) * mm});
            skLineSegment(sketch, "E709", {"start": v(98.56, -170.14) * mm, "end": v(99.24, -169.74) * mm});
            skLineSegment(sketch, "E710", {"start": v(98.56, -170.14) * mm, "end": v(98.73, -170.24) * mm});
            skLineSegment(sketch, "E711", {"start": v(107.15, -171.12) * mm, "end": v(95.36, -171.12) * mm});
            skLineSegment(sketch, "E712", {"start": v(95.36, -170.24) * mm, "end": v(95.36, -171.12) * mm});
            skLineSegment(sketch, "E713", {"start": v(107.15, -170.24) * mm, "end": v(107.15, -171.12) * mm});
            skLineSegment(sketch, "E714", {"start": v(104.92, -174.54) * mm, "end": v(97.51, -174.54) * mm});
            skLineSegment(sketch, "E715", {"start": v(106.1, -171.12) * mm, "end": v(106.1, -173.47) * mm});
            skLineSegment(sketch, "E716", {"start": v(96.41, -171.12) * mm, "end": v(96.41, -173.47) * mm});
            skLineSegment(sketch, "E717", {"start": v(98.69, -173.47) * mm, "end": v(98.69, -171.12) * mm});
            skLineSegment(sketch, "E718", {"start": v(103.82, -173.47) * mm, "end": v(103.82, -171.12) * mm});
            skArc(sketch, "E719", {"start": v(98.69, -173.47) * mm, "mid": v(101.25, -174.54) * mm, "end": v(103.82, -173.47) * mm});
            skArc(sketch, "E720", {"start": v(103.82, -173.47) * mm, "mid": v(104.95, -174.54) * mm, "end": v(106.1, -173.47) * mm});
            skArc(sketch, "E721", {"start": v(96.41, -173.47) * mm, "mid": v(97.55, -174.54) * mm, "end": v(98.69, -173.47) * mm});
            skLineSegment(sketch, "E722", {"start": v(99.24, -157.29) * mm, "end": v(99.24, -152.35) * mm});
            skLineSegment(sketch, "E723", {"start": v(103.26, -157.29) * mm, "end": v(103.26, -152.35) * mm});
            skLineSegment(sketch, "E724", {"start": v(101.25, -151.19) * mm, "end": v(99.24, -152.35) * mm});
            skLineSegment(sketch, "E725", {"start": v(101.25, -151.19) * mm, "end": v(103.26, -152.35) * mm});
            skLineSegment(sketch, "E726", {"start": v(101.25, -151.19) * mm, "end": v(101.25, -153.73) * mm});
            skArc(sketch, "E727", {"start": v(101.25, -153.73) * mm, "mid": v(101.84, -155.15) * mm, "end": v(103.26, -155.74) * mm});
            skLineSegment(sketch, "E728", {"start": v(-9.09, 41.6) * mm, "end": v(-12.13, 41.6) * mm});
            skLineSegment(sketch, "E729", {"start": v(-12.13, 41.6) * mm, "end": v(-12.13, 56.84) * mm});
            skLineSegment(sketch, "E730", {"start": v(-9.09, 41.6) * mm, "end": v(-9.09, 56.84) * mm});
            skArc(sketch, "E731", {"start": v(-8.32, 57.6) * mm, "mid": v(-8.86, 57.38) * mm, "end": v(-9.09, 56.84) * mm});
            skArc(sketch, "E732", {"start": v(-8.32, 60.65) * mm, "mid": v(-11.02, 59.53) * mm, "end": v(-12.13, 56.84) * mm});
            skLineSegment(sketch, "E733", {"start": v(-8.32, 60.65) * mm, "end": v(40.73, 60.65) * mm});
            skLineSegment(sketch, "E734", {"start": v(-8.32, 57.6) * mm, "end": v(40.73, 57.6) * mm});
            skArc(sketch, "E735", {"start": v(41.5, 56.84) * mm, "mid": v(41.27, 57.38) * mm, "end": v(40.73, 57.6) * mm});
            skArc(sketch, "E736", {"start": v(44.54, 56.84) * mm, "mid": v(43.43, 59.53) * mm, "end": v(40.73, 60.65) * mm});
            skLineSegment(sketch, "E737", {"start": v(44.54, 56.84) * mm, "end": v(44.54, -75.94) * mm});
            skLineSegment(sketch, "E738", {"start": v(41.5, 56.84) * mm, "end": v(41.5, -75.94) * mm});
            skLineSegment(sketch, "E739", {"start": v(98.81, 41.6) * mm, "end": v(101.86, 41.6) * mm});
            skLineSegment(sketch, "E740", {"start": v(101.86, 41.6) * mm, "end": v(101.86, 56.84) * mm});
            skLineSegment(sketch, "E741", {"start": v(98.81, 41.6) * mm, "end": v(98.81, 56.84) * mm});
            skArc(sketch, "E742", {"start": v(98.81, 56.84) * mm, "mid": v(98.59, 57.38) * mm, "end": v(98.05, 57.6) * mm});
            skArc(sketch, "E743", {"start": v(101.86, 56.84) * mm, "mid": v(100.74, 59.53) * mm, "end": v(98.05, 60.65) * mm});
            skLineSegment(sketch, "E744", {"start": v(98.05, 60.65) * mm, "end": v(49, 60.65) * mm});
            skLineSegment(sketch, "E745", {"start": v(98.05, 57.6) * mm, "end": v(49, 57.6) * mm});
            skArc(sketch, "E746", {"start": v(49, 57.6) * mm, "mid": v(48.45, 57.38) * mm, "end": v(48.23, 56.84) * mm});
            skArc(sketch, "E747", {"start": v(49, 60.65) * mm, "mid": v(46.3, 59.53) * mm, "end": v(45.18, 56.84) * mm});
            skLineSegment(sketch, "E748", {"start": v(45.18, 56.84) * mm, "end": v(45.18, -75.94) * mm});
            skLineSegment(sketch, "E749", {"start": v(48.23, 56.84) * mm, "end": v(48.23, -75.94) * mm});
            skLineSegment(sketch, "E750", {"start": v(83.37, -136.63) * mm, "end": v(83.37, -135.36) * mm});
            skLineSegment(sketch, "E751", {"start": v(70.16, -136.63) * mm, "end": v(70.16, -135.36) * mm});
            skLineSegment(sketch, "E752", {"start": v(81.96, -141.05) * mm, "end": v(81.96, -136.63) * mm});
            skLineSegment(sketch, "E753", {"start": v(71.57, -141.05) * mm, "end": v(71.57, -136.63) * mm});
            skLineSegment(sketch, "E754", {"start": v(79.2, -93.54) * mm, "end": v(79.2, -92.52) * mm});
            skLineSegment(sketch, "E755", {"start": v(79.2, -91.73) * mm, "end": v(79.2, -90.7) * mm});
            skLineSegment(sketch, "E756", {"start": v(79.2, -89.92) * mm, "end": v(79.2, -88.9) * mm});
            skLineSegment(sketch, "E757", {"start": v(79.2, -88.1) * mm, "end": v(79.2, -87.08) * mm});
            skLineSegment(sketch, "E758", {"start": v(79.2, -86.3) * mm, "end": v(79.2, -85.27) * mm});
            skLineSegment(sketch, "E759", {"start": v(79.2, -84.48) * mm, "end": v(79.2, -83.46) * mm});
            skLineSegment(sketch, "E760", {"start": v(79.2, -82.66) * mm, "end": v(79.2, -81.64) * mm});
            skLineSegment(sketch, "E761", {"start": v(79.2, -80.85) * mm, "end": v(79.2, -79.83) * mm});
            skLineSegment(sketch, "E762", {"start": v(79.2, -79.04) * mm, "end": v(79.2, -78.01) * mm});
            skLineSegment(sketch, "E763", {"start": v(79.2, -77.22) * mm, "end": v(79.2, -76.2) * mm});
            skLineSegment(sketch, "E764", {"start": v(79.2, -75.4) * mm, "end": v(79.2, -74.39) * mm});
            skLineSegment(sketch, "E765", {"start": v(74.32, -95.36) * mm, "end": v(74.32, -94.34) * mm});
            skLineSegment(sketch, "E766", {"start": v(74.32, -93.54) * mm, "end": v(74.32, -92.52) * mm});
            skLineSegment(sketch, "E767", {"start": v(74.32, -91.73) * mm, "end": v(74.32, -90.7) * mm});
            skLineSegment(sketch, "E768", {"start": v(74.32, -89.92) * mm, "end": v(74.32, -88.9) * mm});
            skLineSegment(sketch, "E769", {"start": v(74.32, -88.1) * mm, "end": v(74.32, -87.08) * mm});
            skLineSegment(sketch, "E770", {"start": v(74.32, -86.3) * mm, "end": v(74.32, -85.27) * mm});
            skLineSegment(sketch, "E771", {"start": v(74.32, -84.48) * mm, "end": v(74.32, -83.46) * mm});
            skLineSegment(sketch, "E772", {"start": v(74.32, -82.66) * mm, "end": v(74.32, -81.64) * mm});
            skLineSegment(sketch, "E773", {"start": v(74.32, -80.85) * mm, "end": v(74.32, -79.83) * mm});
            skLineSegment(sketch, "E774", {"start": v(74.32, -79.04) * mm, "end": v(74.32, -78.01) * mm});
            skLineSegment(sketch, "E775", {"start": v(74.32, -77.22) * mm, "end": v(74.32, -76.2) * mm});
            skLineSegment(sketch, "E776", {"start": v(73.64, -93.94) * mm, "end": v(74.32, -94.34) * mm});
            skLineSegment(sketch, "E777", {"start": v(73.64, -93.94) * mm, "end": v(74.32, -93.54) * mm});
            skLineSegment(sketch, "E778", {"start": v(73.64, -92.13) * mm, "end": v(74.32, -92.52) * mm});
            skLineSegment(sketch, "E779", {"start": v(73.64, -92.13) * mm, "end": v(74.32, -91.73) * mm});
            skLineSegment(sketch, "E780", {"start": v(79.89, -92.13) * mm, "end": v(79.2, -92.52) * mm});
            skLineSegment(sketch, "E781", {"start": v(79.89, -92.13) * mm, "end": v(79.2, -91.73) * mm});
            skLineSegment(sketch, "E782", {"start": v(79.89, -90.31) * mm, "end": v(79.2, -90.7) * mm});
            skLineSegment(sketch, "E783", {"start": v(79.89, -90.31) * mm, "end": v(79.2, -89.92) * mm});
            skLineSegment(sketch, "E784", {"start": v(73.64, -93.94) * mm, "end": v(79.89, -92.13) * mm});
            skLineSegment(sketch, "E785", {"start": v(73.64, -92.13) * mm, "end": v(79.89, -90.31) * mm});
            skLineSegment(sketch, "E786", {"start": v(74.32, -94.34) * mm, "end": v(79.2, -92.52) * mm});
            skLineSegment(sketch, "E787", {"start": v(74.32, -93.54) * mm, "end": v(79.2, -91.73) * mm});
            skLineSegment(sketch, "E788", {"start": v(74.32, -92.52) * mm, "end": v(79.2, -90.7) * mm});
            skLineSegment(sketch, "E789", {"start": v(74.32, -91.73) * mm, "end": v(79.2, -89.92) * mm});
            skLineSegment(sketch, "E790", {"start": v(73.64, -90.31) * mm, "end": v(74.32, -90.7) * mm});
            skLineSegment(sketch, "E791", {"start": v(73.64, -90.31) * mm, "end": v(74.32, -89.92) * mm});
            skLineSegment(sketch, "E792", {"start": v(73.64, -88.5) * mm, "end": v(74.32, -88.9) * mm});
            skLineSegment(sketch, "E793", {"start": v(73.64, -88.5) * mm, "end": v(74.32, -88.1) * mm});
            skLineSegment(sketch, "E794", {"start": v(79.89, -88.5) * mm, "end": v(79.2, -88.9) * mm});
            skLineSegment(sketch, "E795", {"start": v(79.89, -88.5) * mm, "end": v(79.2, -88.1) * mm});
            skLineSegment(sketch, "E796", {"start": v(79.89, -86.69) * mm, "end": v(79.2, -87.08) * mm});
            skLineSegment(sketch, "E797", {"start": v(79.89, -86.69) * mm, "end": v(79.2, -86.3) * mm});
            skLineSegment(sketch, "E798", {"start": v(73.64, -90.31) * mm, "end": v(79.89, -88.5) * mm});
            skLineSegment(sketch, "E799", {"start": v(73.64, -88.5) * mm, "end": v(79.89, -86.69) * mm});
            skLineSegment(sketch, "E800", {"start": v(74.32, -90.7) * mm, "end": v(79.2, -88.9) * mm});
            skLineSegment(sketch, "E801", {"start": v(74.32, -89.92) * mm, "end": v(79.2, -88.1) * mm});
            skLineSegment(sketch, "E802", {"start": v(74.32, -88.9) * mm, "end": v(79.2, -87.08) * mm});
            skLineSegment(sketch, "E803", {"start": v(74.32, -88.1) * mm, "end": v(79.2, -86.3) * mm});
            skLineSegment(sketch, "E804", {"start": v(73.64, -86.69) * mm, "end": v(74.32, -87.08) * mm});
            skLineSegment(sketch, "E805", {"start": v(73.64, -86.69) * mm, "end": v(74.32, -86.3) * mm});
            skLineSegment(sketch, "E806", {"start": v(79.89, -84.87) * mm, "end": v(79.2, -85.27) * mm});
            skLineSegment(sketch, "E807", {"start": v(79.89, -84.87) * mm, "end": v(79.2, -84.48) * mm});
            skLineSegment(sketch, "E808", {"start": v(73.64, -86.69) * mm, "end": v(79.89, -84.87) * mm});
            skLineSegment(sketch, "E809", {"start": v(74.32, -87.08) * mm, "end": v(79.2, -85.27) * mm});
            skLineSegment(sketch, "E810", {"start": v(74.32, -86.3) * mm, "end": v(79.2, -84.48) * mm});
            skLineSegment(sketch, "E811", {"start": v(73.64, -84.87) * mm, "end": v(74.32, -85.27) * mm});
            skLineSegment(sketch, "E812", {"start": v(73.64, -84.87) * mm, "end": v(74.32, -84.48) * mm});
            skLineSegment(sketch, "E813", {"start": v(73.64, -83.06) * mm, "end": v(74.32, -83.46) * mm});
            skLineSegment(sketch, "E814", {"start": v(73.64, -83.06) * mm, "end": v(74.32, -82.66) * mm});
            skLineSegment(sketch, "E815", {"start": v(79.89, -83.06) * mm, "end": v(79.2, -83.46) * mm});
            skLineSegment(sketch, "E816", {"start": v(79.89, -83.06) * mm, "end": v(79.2, -82.66) * mm});
            skLineSegment(sketch, "E817", {"start": v(79.89, -81.25) * mm, "end": v(79.2, -81.64) * mm});
            skLineSegment(sketch, "E818", {"start": v(79.89, -81.25) * mm, "end": v(79.2, -80.85) * mm});
            skLineSegment(sketch, "E819", {"start": v(73.64, -84.87) * mm, "end": v(79.89, -83.06) * mm});
            skLineSegment(sketch, "E820", {"start": v(73.64, -83.06) * mm, "end": v(79.89, -81.25) * mm});
            skLineSegment(sketch, "E821", {"start": v(74.32, -85.27) * mm, "end": v(79.2, -83.46) * mm});
            skLineSegment(sketch, "E822", {"start": v(74.32, -84.48) * mm, "end": v(79.2, -82.66) * mm});
            skLineSegment(sketch, "E823", {"start": v(74.32, -83.46) * mm, "end": v(79.2, -81.64) * mm});
            skLineSegment(sketch, "E824", {"start": v(74.32, -82.66) * mm, "end": v(79.2, -80.85) * mm});
            skLineSegment(sketch, "E825", {"start": v(73.64, -81.25) * mm, "end": v(74.32, -81.64) * mm});
            skLineSegment(sketch, "E826", {"start": v(73.64, -81.25) * mm, "end": v(74.32, -80.85) * mm});
            skLineSegment(sketch, "E827", {"start": v(73.64, -79.43) * mm, "end": v(74.32, -79.83) * mm});
            skLineSegment(sketch, "E828", {"start": v(73.64, -79.43) * mm, "end": v(74.32, -79.04) * mm});
            skLineSegment(sketch, "E829", {"start": v(79.89, -79.43) * mm, "end": v(79.2, -79.83) * mm});
            skLineSegment(sketch, "E830", {"start": v(79.89, -79.43) * mm, "end": v(79.2, -79.04) * mm});
            skLineSegment(sketch, "E831", {"start": v(79.89, -77.62) * mm, "end": v(79.2, -78.01) * mm});
            skLineSegment(sketch, "E832", {"start": v(79.89, -77.62) * mm, "end": v(79.2, -77.22) * mm});
            skLineSegment(sketch, "E833", {"start": v(73.64, -81.25) * mm, "end": v(79.89, -79.43) * mm});
            skLineSegment(sketch, "E834", {"start": v(73.64, -79.43) * mm, "end": v(79.89, -77.62) * mm});
            skLineSegment(sketch, "E835", {"start": v(74.32, -81.64) * mm, "end": v(79.2, -79.83) * mm});
            skLineSegment(sketch, "E836", {"start": v(74.32, -80.85) * mm, "end": v(79.2, -79.04) * mm});
            skLineSegment(sketch, "E837", {"start": v(74.32, -79.83) * mm, "end": v(79.2, -78.01) * mm});
            skLineSegment(sketch, "E838", {"start": v(74.32, -79.04) * mm, "end": v(79.2, -77.22) * mm});
            skLineSegment(sketch, "E839", {"start": v(73.64, -77.62) * mm, "end": v(74.32, -78.01) * mm});
            skLineSegment(sketch, "E840", {"start": v(73.64, -77.62) * mm, "end": v(74.32, -77.22) * mm});
            skLineSegment(sketch, "E841", {"start": v(73.64, -75.8) * mm, "end": v(74.32, -76.2) * mm});
            skLineSegment(sketch, "E842", {"start": v(73.64, -75.8) * mm, "end": v(74.32, -75.4) * mm});
            skLineSegment(sketch, "E843", {"start": v(79.89, -75.8) * mm, "end": v(79.2, -76.2) * mm});
            skLineSegment(sketch, "E844", {"start": v(79.89, -75.8) * mm, "end": v(79.2, -75.4) * mm});
            skLineSegment(sketch, "E845", {"start": v(79.89, -74) * mm, "end": v(79.2, -74.39) * mm});
            skLineSegment(sketch, "E846", {"start": v(79.89, -74) * mm, "end": v(79.2, -73.6) * mm});
            skLineSegment(sketch, "E847", {"start": v(73.64, -77.62) * mm, "end": v(79.89, -75.8) * mm});
            skLineSegment(sketch, "E848", {"start": v(73.64, -75.8) * mm, "end": v(79.89, -74) * mm});
            skLineSegment(sketch, "E849", {"start": v(74.32, -78.01) * mm, "end": v(79.2, -76.2) * mm});
            skLineSegment(sketch, "E850", {"start": v(74.32, -77.22) * mm, "end": v(79.2, -75.4) * mm});
            skLineSegment(sketch, "E851", {"start": v(74.32, -76.2) * mm, "end": v(79.2, -74.39) * mm});
            skLineSegment(sketch, "E852", {"start": v(74.32, -75.4) * mm, "end": v(79.2, -73.6) * mm});
            skLineSegment(sketch, "E853", {"start": v(70.16, -135.36) * mm, "end": v(83.37, -135.36) * mm});
            skLineSegment(sketch, "E854", {"start": v(70.16, -136.63) * mm, "end": v(83.37, -136.63) * mm});
            skLineSegment(sketch, "E855", {"start": v(72.26, -141.45) * mm, "end": v(81.26, -141.45) * mm});
            skLineSegment(sketch, "E856", {"start": v(74.16, -141.05) * mm, "end": v(74.16, -136.63) * mm});
            skLineSegment(sketch, "E857", {"start": v(79.36, -141.05) * mm, "end": v(79.36, -136.63) * mm});
            skLineSegment(sketch, "E858", {"start": v(72.26, -141.45) * mm, "end": v(71.57, -141.05) * mm});
            skLineSegment(sketch, "E859", {"start": v(81.26, -141.45) * mm, "end": v(81.96, -141.05) * mm});
            skLineSegment(sketch, "E860", {"start": v(78.66, -141.45) * mm, "end": v(79.36, -141.05) * mm});
            skLineSegment(sketch, "E861", {"start": v(73.47, -141.45) * mm, "end": v(74.16, -141.05) * mm});
            skLineSegment(sketch, "E862", {"start": v(80.05, -141.45) * mm, "end": v(79.36, -141.05) * mm});
            skLineSegment(sketch, "E863", {"start": v(74.86, -141.45) * mm, "end": v(74.16, -141.05) * mm});
            skLineSegment(sketch, "E864", {"start": v(74.32, -75.4) * mm, "end": v(74.32, -63.93) * mm});
            skLineSegment(sketch, "E865", {"start": v(78.55, -73.84) * mm, "end": v(78.55, -63.93) * mm});
            skLineSegment(sketch, "E866", {"start": v(76.44, -62.7) * mm, "end": v(74.32, -63.93) * mm});
            skLineSegment(sketch, "E867", {"start": v(76.44, -62.7) * mm, "end": v(78.55, -63.93) * mm});
            skLineSegment(sketch, "E868", {"start": v(76.44, -62.7) * mm, "end": v(76.44, -72.23) * mm});
            skArc(sketch, "E869", {"start": v(76.44, -72.23) * mm, "mid": v(76.77, -73.38) * mm, "end": v(77.68, -74.16) * mm});
            skLineSegment(sketch, "E870", {"start": v(73.64, -95.75) * mm, "end": v(74.32, -96.15) * mm});
            skLineSegment(sketch, "E871", {"start": v(73.64, -95.75) * mm, "end": v(74.32, -95.36) * mm});
            skLineSegment(sketch, "E872", {"start": v(79.89, -93.94) * mm, "end": v(79.2, -94.34) * mm});
            skLineSegment(sketch, "E873", {"start": v(79.89, -93.94) * mm, "end": v(79.2, -93.54) * mm});
            skLineSegment(sketch, "E874", {"start": v(73.64, -95.75) * mm, "end": v(79.89, -93.94) * mm});
            skLineSegment(sketch, "E875", {"start": v(74.32, -96.15) * mm, "end": v(79.2, -94.34) * mm});
            skLineSegment(sketch, "E876", {"start": v(74.32, -95.36) * mm, "end": v(79.2, -93.54) * mm});
            skLineSegment(sketch, "E877", {"start": v(74.32, -96.15) * mm, "end": v(74.32, -135.36) * mm});
            skLineSegment(sketch, "E878", {"start": v(79.2, -94.34) * mm, "end": v(79.2, -135.36) * mm});
            skSolve(sketch);
        }
        {
            var Q0;
            Q0=makeQuery(id+"F0.imprint","IMPRINT",FACE,{"disambiguationData":[TD([[makeQuery(id+"F0.imprint","IMPRINT",EDGE,{"derivedFrom":sQuery(id+"F0.wireOp",EDGE,"E376")}),1.0]])]});
            extrude(context, id + "F1", {"entities" : qUnion([Q0]), "depth" : 2438.4 * mm});
        }
        {
            var Q0;
            Q0=makeQuery(id+"F1.opExtrude","SWEPT_FACE",FACE,{"disambiguationData":[OSD([sQuery(id+"F0.wireOp",EDGE,"E733")])]});
            var sketch = newSketch(context, id + "F2", { "sketchPlane" : qUnion([Q0])});
            skLineSegment(sketch, "E879", {"start": v(-8.32, 0) * mm, "end": v(40.73, 0) * mm});
            skLineSegment(sketch, "E880", {"start": v(16.2, 0) * mm, "end": v(16.2, -9.66) * mm});
            skLineSegment(sketch, "E881", {"start": v(16.2, -9.66) * mm, "end": v(16.2, -464.72) * mm});
            skPoint(sketch, "E882.endSnap0", {"position": v(16.2, -692.25) * mm});
            skCircle(sketch, "E883", {"center": v(16.2, -464.72) * mm, "radius": 3.18 * mm});
            skSolve(sketch);
        }
        {
            var Q0;
            Q0=makeQuery(id+"F2.imprint","IMPRINT",FACE,{"disambiguationData":[TD([[makeQuery(id+"F2.imprint","IMPRINT",EDGE,{"derivedFrom":sQuery(id+"F2.wireOp",EDGE,"E883")}),1.0]])]});
            var Q1;
            Q1=makeQuery(id+"F1.opExtrude","SWEPT_FACE",FACE,{"disambiguationData":[OSD([sQuery(id+"F0.wireOp",EDGE,"E734")])]});
            extrude(context, id + "F3", {"entities" : qUnion([Q0]), "operationType" : NewBodyOperationType.REMOVE, "oppositeDirection" : true, "endBoundEntityFace" : qUnion([Q1]), "depth" : 3.17 * mm});
        }
    });
